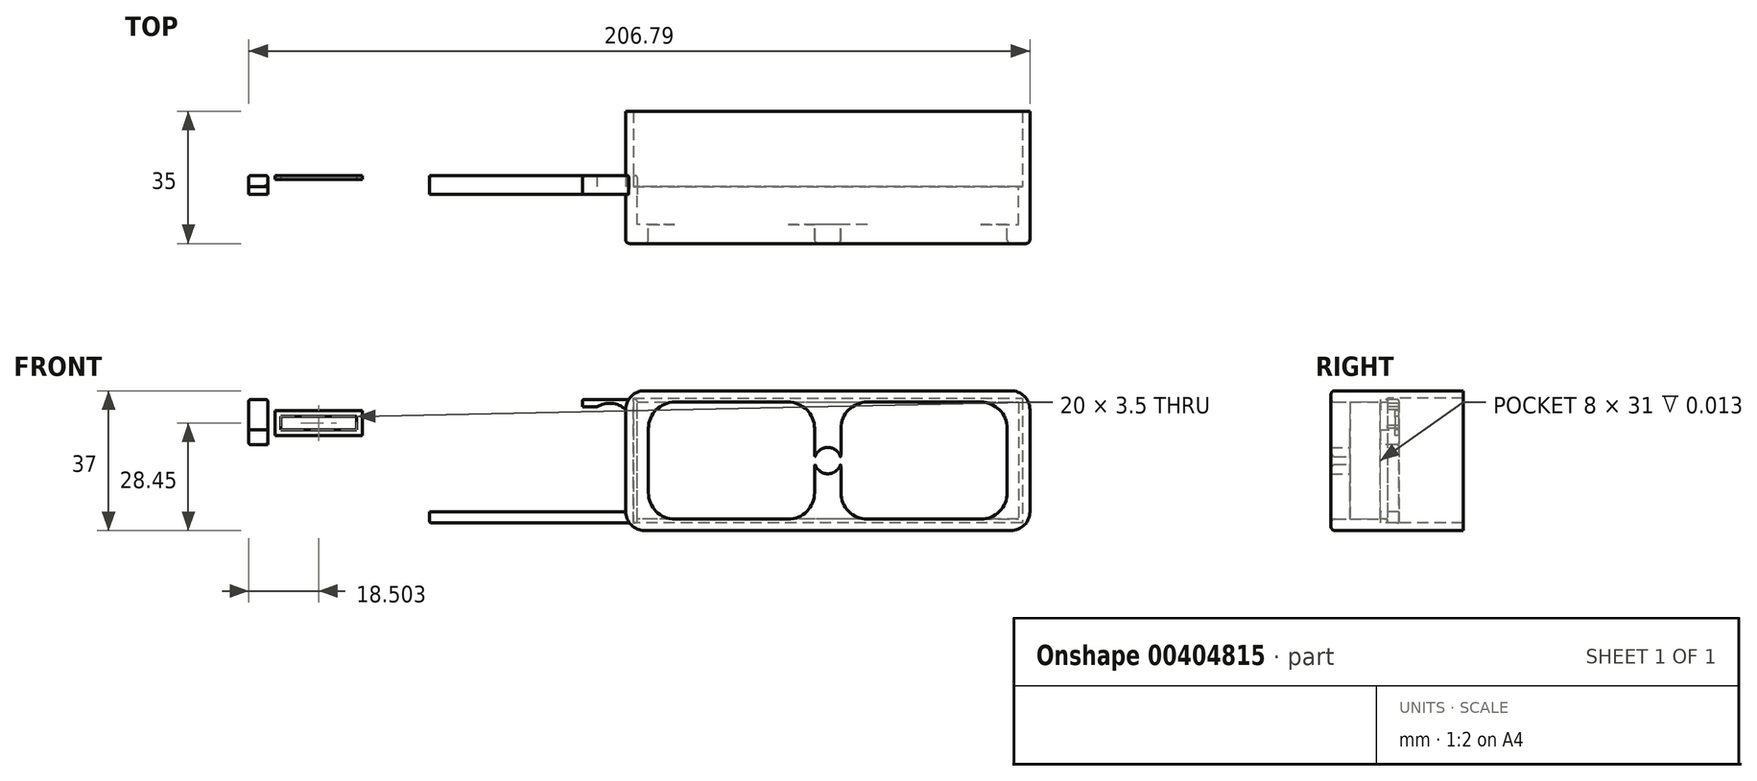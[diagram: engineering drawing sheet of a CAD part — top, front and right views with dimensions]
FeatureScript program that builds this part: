
annotation { "Feature Type Name" : "Feature", "Feature Type Description" : "" }
export const myFeature = defineFeature(function(context is Context, id is Id, definition is map)
    precondition{}
    {
        {
            var Q0;
            Q0=qCreatedBy(makeId("Front.planeOp"),FACE);
            var sketch = newSketch(context, id + "F0", { "sketchPlane" : qUnion([Q0])});
            skLineSegment(sketch, "E0", {"start": v(0, 0) * mm, "end": v(0, 33) * mm});
            skLineSegment(sketch, "E1", {"start": v(0, 33) * mm, "end": v(103, 33) * mm});
            skLineSegment(sketch, "E2", {"start": v(103, 33) * mm, "end": v(103, 0) * mm});
            skLineSegment(sketch, "E3", {"start": v(103, 0) * mm, "end": v(0, 0) * mm});
            skLineSegment(sketch, "E4.0", {"start": v(-2, -2) * mm, "end": v(-2, 35) * mm});
            skLineSegment(sketch, "E4.1", {"start": v(105, -2) * mm, "end": v(-2, -2) * mm});
            skLineSegment(sketch, "E4.2", {"start": v(105, 35) * mm, "end": v(105, -2) * mm});
            skLineSegment(sketch, "E4.3", {"start": v(-2, 35) * mm, "end": v(105, 35) * mm});
            skLineSegment(sketch, "E5", {"start": v(105, 35) * mm, "end": v(56.95, 35) * mm});
            skLineSegment(sketch, "E6", {"start": v(51.5, 33) * mm, "end": v(51.5, 20) * mm});
            skArc(sketch, "E7", {"start": v(54.85, 17.5) * mm, "mid": v(51.5, 20) * mm, "end": v(48.15, 17.5) * mm});
            skLineSegment(sketch, "E8", {"start": v(48, 17.5) * mm, "end": v(48, 25) * mm});
            skLineSegment(sketch, "E9.MirrorCS", {"start": v(55, 17.5) * mm, "end": v(55, 25) * mm});
            skLineSegment(sketch, "E10", {"start": v(48, 15.5) * mm, "end": v(48, 8) * mm});
            skLineSegment(sketch, "E11", {"start": v(55, 15.5) * mm, "end": v(55, 8) * mm});
            skLineSegment(sketch, "E12.0", {"start": v(48, 15.5) * mm, "end": v(48.15, 15.5) * mm});
            skLineSegment(sketch, "E13.0", {"start": v(48, 17.5) * mm, "end": v(48.15, 17.5) * mm});
            skArc(sketch, "E14.trimOffspring", {"start": v(48.15, 15.5) * mm, "mid": v(51.5, 13) * mm, "end": v(54.85, 15.5) * mm});
            skLineSegment(sketch, "E15.trimOffspring", {"start": v(54.85, 15.5) * mm, "end": v(55, 15.5) * mm});
            skLineSegment(sketch, "E16.trimOffspring", {"start": v(51.5, 13) * mm, "end": v(51.5, 0) * mm});
            skPoint(sketch, "E17.orphan", {"position": v(48, 16.5) * mm});
            skPoint(sketch, "E18.end.orphan", {"position": v(55, 16.5) * mm});
            skLineSegment(sketch, "E19.trimOffspring", {"start": v(54.85, 17.5) * mm, "end": v(55, 17.5) * mm});
            skLineSegment(sketch, "E20.0", {"start": v(11, 32) * mm, "end": v(41, 32) * mm});
            skLineSegment(sketch, "E20.1", {"start": v(1, 1) * mm, "end": v(1, 32) * mm});
            skLineSegment(sketch, "E20.2", {"start": v(92, 1) * mm, "end": v(62, 1) * mm});
            skLineSegment(sketch, "E20.3", {"start": v(102, 32) * mm, "end": v(102, 1) * mm});
            skLineSegment(sketch, "E21.0", {"start": v(4, 8) * mm, "end": v(4, 25) * mm});
            skLineSegment(sketch, "E22.0", {"start": v(99, 25) * mm, "end": v(99, 8) * mm});
            skArc(sketch, "E23.filletArc", {"start": v(99, 25) * mm, "mid": v(96.95, 29.95) * mm, "end": v(92, 32) * mm});
            skArc(sketch, "E24.filletArc", {"start": v(92, 1) * mm, "mid": v(96.95, 3.05) * mm, "end": v(99, 8) * mm});
            skLineSegment(sketch, "E25.trimOffspring", {"start": v(62, 32) * mm, "end": v(92, 32) * mm});
            skLineSegment(sketch, "E26.trimOffspring", {"start": v(41, 1) * mm, "end": v(11, 1) * mm});
            skArc(sketch, "E27.filletArc", {"start": v(55, 8) * mm, "mid": v(57.05, 3.05) * mm, "end": v(62, 1) * mm});
            skPoint(sketch, "E28.newPointA", {"position": v(55, 33) * mm});
            skArc(sketch, "E28.filletArc", {"start": v(62, 32) * mm, "mid": v(57.05, 29.95) * mm, "end": v(55, 25) * mm});
            skPoint(sketch, "E29.newPointA", {"position": v(48, 33) * mm});
            skArc(sketch, "E29.filletArc", {"start": v(48, 25) * mm, "mid": v(45.95, 29.95) * mm, "end": v(41, 32) * mm});
            skPoint(sketch, "E30.newPointA", {"position": v(48, 0) * mm});
            skArc(sketch, "E30.filletArc", {"start": v(41, 1) * mm, "mid": v(45.95, 3.05) * mm, "end": v(48, 8) * mm});
            skArc(sketch, "E31.filletArc", {"start": v(4, 8) * mm, "mid": v(6.05, 3.05) * mm, "end": v(11, 1) * mm});
            skArc(sketch, "E32.filletArc", {"start": v(11, 32) * mm, "mid": v(6.05, 29.95) * mm, "end": v(4, 25) * mm});
            skLineSegment(sketch, "E33", {"start": v(92, 1) * mm, "end": v(102, 1) * mm});
            skLineSegment(sketch, "E34", {"start": v(92, 32) * mm, "end": v(102, 32) * mm});
            skLineSegment(sketch, "E35", {"start": v(11, 1) * mm, "end": v(1, 1) * mm});
            skLineSegment(sketch, "E36", {"start": v(1, 32) * mm, "end": v(11, 32) * mm});
            skLineSegment(sketch, "E37", {"start": v(41, 32) * mm, "end": v(62, 32) * mm});
            skLineSegment(sketch, "E38", {"start": v(62, 1) * mm, "end": v(41, 1) * mm});
            skSolve(sketch);
        }
        {
            var Q0;
            Q0=makeQuery(id+"F0.imprint","IMPRINT",FACE,{"disambiguationData":[TD([[makeQuery(id+"F0.imprint","IMPRINT",EDGE,{"derivedFrom":sQuery(id+"F0.wireOp",EDGE,"E0")}),1.0]])]});
            extrude(context, id + "F1", {"entities" : qUnion([Q0]), "oppositeDirection" : true, "depth" : 20 * mm});
        }
        {
            var Q0;
            Q0=makeQuery(id+"F0.imprint","IMPRINT",FACE,{"disambiguationData":[TD([[makeQuery(id+"F0.imprint","IMPRINT",EDGE,{"derivedFrom":sQuery(id+"F0.wireOp",EDGE,"E0")}),1.0]])]});
            var Q1;
            Q1=makeQuery(id+"F0.imprint","IMPRINT",FACE,{"disambiguationData":[TD([[makeQuery(id+"F0.imprint","IMPRINT",EDGE,{"derivedFrom":sQuery(id+"F0.wireOp",EDGE,"E0")}),-1.0]])]});
            var Q2;
            {var subQ0=sQuery(id+"F0.wireOp",EDGE,"E13.0");Q2=makeQuery(id+"F0.imprint","IMPRINT",FACE,{"disambiguationData":[TD([[makeQuery(id+"F0.imprint","IMPRINT",EDGE,{"derivedFrom":subQ0}),1.0]])]});}
            var Q3;
            {var subQ3=sQuery(id+"F0.wireOp",EDGE,"E19.trimOffspring");Q3=makeQuery(id+"F0.imprint","IMPRINT",FACE,{"disambiguationData":[TD([[makeQuery(id+"F0.imprint","IMPRINT",EDGE,{"derivedFrom":subQ3}),1.0]])]});}
            var Q4;
            {var subQ0=sQuery(id+"F0.wireOp",EDGE,"E6");var subQ1=sQuery(id+"F0.wireOp",EDGE,"E1");var subQ2=makeQuery(id+"F0.imprint","INTERSECT",VERTEX,{"derivedFrom":[subQ1,subQ0]});Q4=makeQuery(id+"F0.imprint","IMPRINT",FACE,{"disambiguationData":[TD([[makeQuery(id+"F0.imprint","IMPRINT",EDGE,{"disambiguationData":[TD([[subQ2,1.0]])],"derivedFrom":subQ1}),-1.0]])]});}
            var Q5;
            {var subQ0=sQuery(id+"F0.wireOp",EDGE,"E6");var subQ1=sQuery(id+"F0.wireOp",EDGE,"E1");var subQ2=makeQuery(id+"F0.imprint","INTERSECT",VERTEX,{"derivedFrom":[subQ1,subQ0]});Q5=makeQuery(id+"F0.imprint","IMPRINT",FACE,{"disambiguationData":[TD([[makeQuery(id+"F0.imprint","IMPRINT",EDGE,{"disambiguationData":[TD([[subQ2,-1.0]])],"derivedFrom":subQ1}),-1.0]])]});}
            var Q6;
            {var subQ1=sQuery(id+"F0.wireOp",EDGE,"E2");Q6=makeQuery(id+"F0.imprint","IMPRINT",FACE,{"disambiguationData":[TD([[makeQuery(id+"F0.imprint","IMPRINT",EDGE,{"derivedFrom":subQ1}),-1.0]])]});}
            var Q7;
            {var subQ0=sQuery(id+"F0.wireOp",EDGE,"E11");var subQ1=sQuery(id+"F0.wireOp",EDGE,"E3");var subQ2=makeQuery(id+"F0.imprint","INTERSECT",VERTEX,{"derivedFrom":[subQ1,subQ0]});Q7=makeQuery(id+"F0.imprint","IMPRINT",FACE,{"disambiguationData":[TD([[makeQuery(id+"F0.imprint","IMPRINT",EDGE,{"disambiguationData":[TD([[subQ2,-1.0]])],"derivedFrom":subQ1}),-1.0]])]});}
            var Q8;
            {var subQ0=sQuery(id+"F0.wireOp",EDGE,"E10");var subQ1=sQuery(id+"F0.wireOp",EDGE,"E3");var subQ2=makeQuery(id+"F0.imprint","INTERSECT",VERTEX,{"derivedFrom":[subQ1,subQ0]});Q8=makeQuery(id+"F0.imprint","IMPRINT",FACE,{"disambiguationData":[TD([[makeQuery(id+"F0.imprint","IMPRINT",EDGE,{"disambiguationData":[TD([[subQ2,1.0]])],"derivedFrom":subQ1}),-1.0]])]});}
            var Q9;
            {var subQ1=sQuery(id+"F0.wireOp",EDGE,"E12.0");Q9=makeQuery(id+"F0.imprint","IMPRINT",FACE,{"disambiguationData":[TD([[makeQuery(id+"F0.imprint","IMPRINT",EDGE,{"derivedFrom":subQ1}),-1.0]])]});}
            var Q10;
            {var subQ0=sQuery(id+"F0.wireOp",EDGE,"E15.trimOffspring");Q10=makeQuery(id+"F0.imprint","IMPRINT",FACE,{"disambiguationData":[TD([[makeQuery(id+"F0.imprint","IMPRINT",EDGE,{"derivedFrom":subQ0}),-1.0]])]});}
            var Q11;
            {var subQ3=sQuery(id+"F0.wireOp",EDGE,"E9.MirrorCS");var subQ5=sQuery(id+"F0.wireOp",EDGE,"c4ed635b-4b4c-45bc-97a5-dd19808a82bc.0");var subQ6=makeQuery(id+"F0.imprint","INTERSECT",VERTEX,{"derivedFrom":[subQ5,subQ3]});Q11=makeQuery(id+"F0.imprint","IMPRINT",FACE,{"disambiguationData":[TD([[makeQuery(id+"F0.imprint","IMPRINT",EDGE,{"disambiguationData":[TD([[subQ6,-1.0]])],"derivedFrom":subQ5}),1.0]])]});}
            var Q12;
            {var subQ0=sQuery(id+"F0.wireOp",EDGE,"mgFIaH3y-DYaz-jSyi-80Px-iEue0ywse0mG");Q12=makeQuery(id+"F0.imprint","IMPRINT",FACE,{"disambiguationData":[TD([[makeQuery(id+"F0.imprint","IMPRINT",EDGE,{"derivedFrom":subQ0}),1.0]])]});}
            var Q13;
            {var subQ0=sQuery(id+"F0.wireOp",EDGE,"TVL4aVtS-kMOh-BYX0-d90f-hvQNaALXqrT4");var subQ1=sQuery(id+"F0.wireOp",EDGE,"c4ed635b-4b4c-45bc-97a5-dd19808a82bc.0");var subQ2=makeQuery(id+"F0.imprint","INTERSECT",VERTEX,{"disambiguationData":[OD(0.0)],"derivedFrom":[subQ1,subQ0]});Q13=makeQuery(id+"F0.imprint","IMPRINT",FACE,{"disambiguationData":[TD([[makeQuery(id+"F0.imprint","IMPRINT",EDGE,{"disambiguationData":[TD([[subQ2,-1.0]])],"derivedFrom":subQ1}),1.0]])]});}
            var Q14;
            {var subQ0=sQuery(id+"F0.wireOp",EDGE,"iUmxAfeH-Jdle-Fr7V-BVZL-PfV18QycgyKM");var subQ1=sQuery(id+"F0.wireOp",EDGE,"c4ed635b-4b4c-45bc-97a5-dd19808a82bc.0");var subQ2=makeQuery(id+"F0.imprint","INTERSECT",VERTEX,{"derivedFrom":[subQ1,subQ0]});Q14=makeQuery(id+"F0.imprint","IMPRINT",FACE,{"disambiguationData":[TD([[makeQuery(id+"F0.imprint","IMPRINT",EDGE,{"disambiguationData":[TD([[subQ2,-1.0]])],"derivedFrom":subQ1}),1.0]])]});}
            var Q15;
            {var subQ0=sQuery(id+"F0.wireOp",EDGE,"TVL4aVtS-kMOh-BYX0-d90f-hvQNaALXqrT4");var subQ1=sQuery(id+"F0.wireOp",EDGE,"a24374ab-3477-4681-9d0b-ab59828270b6.0");var subQ2=makeQuery(id+"F0.imprint","INTERSECT",VERTEX,{"disambiguationData":[OD(0.0)],"derivedFrom":[subQ1,subQ0]});Q15=makeQuery(id+"F0.imprint","IMPRINT",FACE,{"disambiguationData":[TD([[makeQuery(id+"F0.imprint","IMPRINT",EDGE,{"disambiguationData":[TD([[subQ2,-1.0]])],"derivedFrom":subQ1}),1.0]])]});}
            var Q16;
            {var subQ9=sQuery(id+"F0.wireOp",EDGE,"yKWUyqlz-4vPE-V50E-0xoB-uYDKYFQVyidN");Q16=makeQuery(id+"F0.imprint","IMPRINT",FACE,{"disambiguationData":[TD([[makeQuery(id+"F0.imprint","IMPRINT",EDGE,{"derivedFrom":subQ9}),1.0]])]});}
            var Q17;
            {var subQ0=sQuery(id+"F0.wireOp",EDGE,"E20.1");Q17=makeQuery(id+"F0.imprint","IMPRINT",FACE,{"disambiguationData":[TD([[makeQuery(id+"F0.imprint","IMPRINT",EDGE,{"derivedFrom":subQ0}),-1.0]])]});}
            var Q18;
            Q18=makeQuery(id+"F0.imprint","IMPRINT",FACE,{"disambiguationData":[TD([[makeQuery(id+"F0.imprint","IMPRINT",EDGE,{"derivedFrom":sQuery(id+"F0.wireOp",EDGE,"E20.3")}),-1.0]])]});
            extrude(context, id + "F2", {"entities" : qUnion([Q0, Q1, Q2, Q3, Q4, Q5, Q6, Q7, Q8, Q9, Q10, Q11, Q12, Q13, Q14, Q15, Q16, Q17, Q18]), "operationType" : NewBodyOperationType.ADD, "depth" : 15 * mm});
        }
        {
            var Q0;
            {var subQ1=sQuery(id+"F0.wireOp",EDGE,"E12.0");Q0=makeQuery(id+"F0.imprint","IMPRINT",FACE,{"disambiguationData":[TD([[makeQuery(id+"F0.imprint","IMPRINT",EDGE,{"derivedFrom":subQ1}),-1.0]])]});}
            var Q1;
            {var subQ5=sQuery(id+"F0.wireOp",EDGE,"E15.trimOffspring");Q1=makeQuery(id+"F0.imprint","IMPRINT",FACE,{"disambiguationData":[TD([[makeQuery(id+"F0.imprint","IMPRINT",EDGE,{"derivedFrom":subQ5}),-1.0]])]});}
            var Q2;
            {var subQ0=sQuery(id+"F0.wireOp",EDGE,"E19.trimOffspring");Q2=makeQuery(id+"F0.imprint","IMPRINT",FACE,{"disambiguationData":[TD([[makeQuery(id+"F0.imprint","IMPRINT",EDGE,{"derivedFrom":subQ0}),1.0]])]});}
            var Q3;
            {var subQ0=sQuery(id+"F0.wireOp",EDGE,"E13.0");Q3=makeQuery(id+"F0.imprint","IMPRINT",FACE,{"disambiguationData":[TD([[makeQuery(id+"F0.imprint","IMPRINT",EDGE,{"derivedFrom":subQ0}),1.0]])]});}
            var Q4;
            {var subQ0=sQuery(id+"F0.wireOp",EDGE,"E12.0");Q4=makeQuery(id+"F0.imprint","IMPRINT",FACE,{"disambiguationData":[TD([[makeQuery(id+"F0.imprint","IMPRINT",EDGE,{"derivedFrom":subQ0}),1.0]])]});}
            var Q5;
            Q5=makeQuery(id+"F0.imprint","IMPRINT",FACE,{"disambiguationData":[TD([[makeQuery(id+"F0.imprint","IMPRINT",EDGE,{"derivedFrom":sQuery(id+"F0.wireOp",EDGE,"E20.3")}),-1.0]])]});
            var Q6;
            Q6=makeQuery(id+"F0.imprint","IMPRINT",FACE,{"disambiguationData":[TD([[makeQuery(id+"F0.imprint","IMPRINT",EDGE,{"derivedFrom":sQuery(id+"F0.wireOp",EDGE,"E20.1")}),-1.0]])]});
            extrude(context, id + "F3", {"entities" : qUnion([Q0, Q1, Q2, Q3, Q4, Q5, Q6]), "operationType" : NewBodyOperationType.REMOVE, "depth" : 10 * mm});
        }
        {
            var Q0;
            Q0=makeQuery(id+"F2.opExtrude","SWEPT_EDGE",EDGE,{"disambiguationData":[OSD([sQuery(id+"F0.wireOp",EDGE,"E20.0"),sQuery(id+"F0.wireOp",EDGE,"E20.1")])]});
            var Q1;
            Q1=makeQuery(id+"F2.opExtrude","SWEPT_EDGE",EDGE,{"disambiguationData":[OSD([sQuery(id+"F0.wireOp",EDGE,"E8"),sQuery(id+"F0.wireOp",EDGE,"E20.0")])]});
            var Q2;
            Q2=makeQuery(id+"F2.opExtrude","SWEPT_EDGE",EDGE,{"disambiguationData":[OSD([sQuery(id+"F0.wireOp",EDGE,"E11"),sQuery(id+"F0.wireOp",EDGE,"E20.2")])]});
            var Q3;
            Q3=makeQuery(id+"F2.opExtrude","SWEPT_EDGE",EDGE,{"disambiguationData":[OSD([sQuery(id+"F0.wireOp",EDGE,"E20.1"),sQuery(id+"F0.wireOp",EDGE,"E20.2")])]});
            var Q4;
            Q4=makeQuery(id+"F2.opExtrude","SWEPT_EDGE",EDGE,{"disambiguationData":[OSD([sQuery(id+"F0.wireOp",EDGE,"E10"),sQuery(id+"F0.wireOp",EDGE,"E20.2")])]});
            var Q5;
            Q5=makeQuery(id+"F2.opExtrude","SWEPT_EDGE",EDGE,{"disambiguationData":[OSD([sQuery(id+"F0.wireOp",EDGE,"E20.2"),sQuery(id+"F0.wireOp",EDGE,"E20.3")])]});
            var Q6;
            Q6=makeQuery(id+"F2.opExtrude","SWEPT_EDGE",EDGE,{"disambiguationData":[OSD([sQuery(id+"F0.wireOp",EDGE,"E20.0"),sQuery(id+"F0.wireOp",EDGE,"E20.3")])]});
            var Q7;
            {var subQ0=sQuery(id+"F0.wireOp",EDGE,"E4.2");var subQ1=sQuery(id+"F0.wireOp",EDGE,"E4.1");Q7=makeQuery(id+"F2.boolean.opBoolean","MERGE",EDGE,{"derivedFrom":[makeQuery(id+"F1.opExtrude","SWEPT_EDGE",EDGE,{"disambiguationData":[OSD([subQ1,subQ0])]}),makeQuery(id+"F2.opExtrude","SWEPT_EDGE",EDGE,{"disambiguationData":[OSD([subQ1,subQ0])]})]});}
            var Q8;
            {var subQ0=sQuery(id+"F0.wireOp",EDGE,"E5");var subQ1=sQuery(id+"F0.wireOp",EDGE,"E4.2");Q8=makeQuery(id+"F2.boolean.opBoolean","MERGE",EDGE,{"derivedFrom":[makeQuery(id+"F1.opExtrude","SWEPT_EDGE",EDGE,{"disambiguationData":[OSD([subQ1,subQ0])]}),makeQuery(id+"F2.opExtrude","SWEPT_EDGE",EDGE,{"disambiguationData":[OSD([subQ1,subQ0])]})]});}
            var Q9;
            {var subQ0=sQuery(id+"F0.wireOp",EDGE,"E4.3");var subQ1=sQuery(id+"F0.wireOp",EDGE,"E4.0");Q9=makeQuery(id+"F2.boolean.opBoolean","MERGE",EDGE,{"derivedFrom":[makeQuery(id+"F1.opExtrude","SWEPT_EDGE",EDGE,{"disambiguationData":[OSD([subQ1,subQ0])]}),makeQuery(id+"F2.opExtrude","SWEPT_EDGE",EDGE,{"disambiguationData":[OSD([subQ1,subQ0])]})]});}
            var Q10;
            {var subQ0=sQuery(id+"F0.wireOp",EDGE,"E4.1");var subQ1=sQuery(id+"F0.wireOp",EDGE,"E4.0");Q10=makeQuery(id+"F2.boolean.opBoolean","MERGE",EDGE,{"derivedFrom":[makeQuery(id+"F1.opExtrude","SWEPT_EDGE",EDGE,{"disambiguationData":[OSD([subQ1,subQ0])]}),makeQuery(id+"F2.opExtrude","SWEPT_EDGE",EDGE,{"disambiguationData":[OSD([subQ1,subQ0])]})]});}
            var Q11;
            Q11=makeQuery(id+"F2.opExtrude","SWEPT_EDGE",EDGE,{"disambiguationData":[OSD([sQuery(id+"F0.wireOp",EDGE,"E9.MirrorCS"),sQuery(id+"F0.wireOp",EDGE,"E20.0")])]});
            fillet(context, id + "F4", {"entities" : qUnion([Q0, Q1, Q2, Q3, Q4, Q5, Q6, Q7, Q8, Q9, Q10, Q11]), "radius" : 5 * mm, "tangentPropagation" : true, "allowEdgeOverflow" : false});
        }
        {
            var Q0;
            Q0=makeQuery(id+"F2.opExtrude","CAP_EDGE",EDGE,{"disambiguationData":[OSD([sQuery(id+"F0.wireOp",EDGE,"E32.filletArc")])],"isStart":false});
            var Q1;
            Q1=makeQuery(id+"F2.opExtrude","CAP_EDGE",EDGE,{"disambiguationData":[OSD([sQuery(id+"F0.wireOp",EDGE,"E28.filletArc")])],"isStart":false});
            var Q2;
            Q2=makeQuery(id+"F2.opExtrude","CAP_EDGE",EDGE,{"disambiguationData":[OSD([sQuery(id+"F0.wireOp",EDGE,"E4.3"),sQuery(id+"F0.wireOp",EDGE,"E5")])],"isStart":false});
            var Q3;
            Q3=makeQuery(id+"F1ZY5U0QfWKgnaE_2.boolean.opBoolean","COPY",EDGE,{"derivedFrom":makeQuery(id+"F1ZY5U0QfWKgnaE_2.opExtrude","CAP_EDGE",EDGE,{"disambiguationData":[OSD([sQuery(id+"FzWsDeid9OxCe4s_2.wireOp",EDGE,"ddf2c67c-9696-4573-b7c7-edc6250c991e.0")])],"isStart":true})});
            var Q4;
            {var subQ0=sQuery(id+"FzWsDeid9OxCe4s_2.wireOp",EDGE,"DHWVtWLh-aHPT-YNDw-NuMh-FcVQlgM1t4xD");Q4=makeQuery(id+"F1ZY5U0QfWKgnaE_2.boolean.opBoolean","COPY",EDGE,{"derivedFrom":makeQuery(id+"F1ZY5U0QfWKgnaE_2.opExtrude","CAP_EDGE",EDGE,{"disambiguationData":[OSD([subQ0]),TDD([makeQuery(id+"FzWsDeid9OxCe4s_2.imprint","IMPRINT",EDGE,{"disambiguationData":[TD([[makeQuery(id+"FzWsDeid9OxCe4s_2.imprint","INTERSECT",VERTEX,{"derivedFrom":[subQ0,sQuery(id+"FzWsDeid9OxCe4s_2.wireOp",EDGE,"ddf2c67c-9696-4573-b7c7-edc6250c991e.0")]}),-1.0]])],"derivedFrom":subQ0})])],"isStart":true})});}
            var Q5;
            {var subQ0=sQuery(id+"FzWsDeid9OxCe4s_2.wireOp",EDGE,"uo2K4ESE-ioYr-gu5B-DHa5-rfcAboMNfEFw");Q5=makeQuery(id+"F1ZY5U0QfWKgnaE_2.boolean.opBoolean","COPY",EDGE,{"derivedFrom":makeQuery(id+"F1ZY5U0QfWKgnaE_2.opExtrude","CAP_EDGE",EDGE,{"disambiguationData":[OSD([subQ0]),TDD([makeQuery(id+"FzWsDeid9OxCe4s_2.imprint","IMPRINT",EDGE,{"disambiguationData":[TD([[makeQuery(id+"FzWsDeid9OxCe4s_2.imprint","INTERSECT",VERTEX,{"derivedFrom":[subQ0,sQuery(id+"FzWsDeid9OxCe4s_2.wireOp",EDGE,"ddf2c67c-9696-4573-b7c7-edc6250c991e.0")]}),1.0]])],"derivedFrom":subQ0})])],"isStart":true})});}
            var Q6;
            Q6=makeQuery(id+"F1ZY5U0QfWKgnaE_2.boolean.opBoolean","COPY",EDGE,{"derivedFrom":makeQuery(id+"F1ZY5U0QfWKgnaE_2.opExtrude","CAP_EDGE",EDGE,{"disambiguationData":[OSD([sQuery(id+"FzWsDeid9OxCe4s_2.wireOp",EDGE,"6cb0e26c-a951-431f-a703-2220c8751553.0")])],"isStart":true})});
            var Q7;
            Q7=makeQuery(id+"F1ZY5U0QfWKgnaE_2.boolean.opBoolean","COPY",EDGE,{"derivedFrom":makeQuery(id+"F1ZY5U0QfWKgnaE_2.opExtrude","CAP_EDGE",EDGE,{"disambiguationData":[OSD([sQuery(id+"FzWsDeid9OxCe4s_2.wireOp",EDGE,"f3bd379a-a156-41d0-9f10-f2bbd5b9d83f.0")])],"isStart":true})});
            var Q8;
            {var subQ0=sQuery(id+"FzWsDeid9OxCe4s_2.wireOp",EDGE,"uo2K4ESE-ioYr-gu5B-DHa5-rfcAboMNfEFw");Q8=makeQuery(id+"F1ZY5U0QfWKgnaE_2.boolean.opBoolean","COPY",EDGE,{"derivedFrom":makeQuery(id+"F1ZY5U0QfWKgnaE_2.opExtrude","CAP_EDGE",EDGE,{"disambiguationData":[OSD([subQ0]),TDD([makeQuery(id+"FzWsDeid9OxCe4s_2.imprint","IMPRINT",EDGE,{"disambiguationData":[TD([[makeQuery(id+"FzWsDeid9OxCe4s_2.imprint","INTERSECT",VERTEX,{"derivedFrom":[subQ0,sQuery(id+"FzWsDeid9OxCe4s_2.wireOp",EDGE,"f3bd379a-a156-41d0-9f10-f2bbd5b9d83f.0")]}),-1.0]])],"derivedFrom":subQ0})])],"isStart":true})});}
            var Q9;
            {var subQ0=sQuery(id+"FzWsDeid9OxCe4s_2.wireOp",EDGE,"DHWVtWLh-aHPT-YNDw-NuMh-FcVQlgM1t4xD");Q9=makeQuery(id+"F1ZY5U0QfWKgnaE_2.boolean.opBoolean","COPY",EDGE,{"derivedFrom":makeQuery(id+"F1ZY5U0QfWKgnaE_2.opExtrude","CAP_EDGE",EDGE,{"disambiguationData":[OSD([subQ0]),TDD([makeQuery(id+"FzWsDeid9OxCe4s_2.imprint","IMPRINT",EDGE,{"disambiguationData":[TD([[makeQuery(id+"FzWsDeid9OxCe4s_2.imprint","INTERSECT",VERTEX,{"derivedFrom":[subQ0,sQuery(id+"FzWsDeid9OxCe4s_2.wireOp",EDGE,"f3bd379a-a156-41d0-9f10-f2bbd5b9d83f.0")]}),1.0]])],"derivedFrom":subQ0})])],"isStart":true})});}
            var Q10;
            Q10=makeQuery(id+"F1ZY5U0QfWKgnaE_2.boolean.opBoolean","COPY",EDGE,{"derivedFrom":makeQuery(id+"F1ZY5U0QfWKgnaE_2.opExtrude","CAP_EDGE",EDGE,{"disambiguationData":[OSD([sQuery(id+"FzWsDeid9OxCe4s_2.wireOp",EDGE,"52b8b0e7-0203-483f-8d4f-d96776e66651.0")])],"isStart":true})});
            var Q11;
            {var subQ0=sQuery(id+"FzWsDeid9OxCe4s_2.wireOp",EDGE,"DHWVtWLh-aHPT-YNDw-NuMh-FcVQlgM1t4xD");var subQ1=sQuery(id+"F0.wireOp",EDGE,"E4.1");Q11=makeQuery(id+"F1ZY5U0QfWKgnaE_2.boolean.opBoolean","INTERSECT",EDGE,{"derivedFrom":[makeQuery(id+"F2.boolean.opBoolean","MERGE",FACE,{"derivedFrom":[makeQuery(id+"F1.opExtrude","SWEPT_FACE",FACE,{"disambiguationData":[OSD([subQ1])]}),makeQuery(id+"F2.opExtrude","SWEPT_FACE",FACE,{"disambiguationData":[OSD([subQ1])]})]}),makeQuery(id+"F1ZY5U0QfWKgnaE_2.opExtrude","SWEPT_FACE",FACE,{"disambiguationData":[OSD([subQ0]),TDD([makeQuery(id+"FzWsDeid9OxCe4s_2.imprint","IMPRINT",EDGE,{"disambiguationData":[TD([[makeQuery(id+"FzWsDeid9OxCe4s_2.imprint","INTERSECT",VERTEX,{"derivedFrom":[subQ0,sQuery(id+"FzWsDeid9OxCe4s_2.wireOp",EDGE,"f3bd379a-a156-41d0-9f10-f2bbd5b9d83f.0")]}),1.0]])],"derivedFrom":subQ0})])]})]});}
            var Q12;
            {var subQ0=sQuery(id+"FzWsDeid9OxCe4s_2.wireOp",EDGE,"DHWVtWLh-aHPT-YNDw-NuMh-FcVQlgM1t4xD");var subQ1=sQuery(id+"F0.wireOp",EDGE,"E4.1");Q12=makeQuery(id+"F1ZY5U0QfWKgnaE_2.boolean.opBoolean","INTERSECT",EDGE,{"derivedFrom":[makeQuery(id+"F2.boolean.opBoolean","MERGE",FACE,{"derivedFrom":[makeQuery(id+"F1.opExtrude","SWEPT_FACE",FACE,{"disambiguationData":[OSD([subQ1])]}),makeQuery(id+"F2.opExtrude","SWEPT_FACE",FACE,{"disambiguationData":[OSD([subQ1])]})]}),makeQuery(id+"F1ZY5U0QfWKgnaE_2.opExtrude","SWEPT_FACE",FACE,{"disambiguationData":[OSD([subQ0]),TDD([makeQuery(id+"FzWsDeid9OxCe4s_2.imprint","IMPRINT",EDGE,{"disambiguationData":[TD([[makeQuery(id+"FzWsDeid9OxCe4s_2.imprint","INTERSECT",VERTEX,{"derivedFrom":[subQ0,sQuery(id+"FzWsDeid9OxCe4s_2.wireOp",EDGE,"f3bd379a-a156-41d0-9f10-f2bbd5b9d83f.0")]}),1.0]])],"derivedFrom":subQ0})])]})]});}
            var Q13;
            {var subQ0=sQuery(id+"F0.wireOp",EDGE,"E4.1");Q13=makeQuery(id+"F1ZY5U0QfWKgnaE_2.boolean.opBoolean","INTERSECT",EDGE,{"derivedFrom":[makeQuery(id+"F2.boolean.opBoolean","MERGE",FACE,{"derivedFrom":[makeQuery(id+"F1.opExtrude","SWEPT_FACE",FACE,{"disambiguationData":[OSD([subQ0])]}),makeQuery(id+"F2.opExtrude","SWEPT_FACE",FACE,{"disambiguationData":[OSD([subQ0])]})]}),makeQuery(id+"F1ZY5U0QfWKgnaE_2.opExtrude","SWEPT_FACE",FACE,{"disambiguationData":[OSD([sQuery(id+"FzWsDeid9OxCe4s_2.wireOp",EDGE,"f3bd379a-a156-41d0-9f10-f2bbd5b9d83f.0")])]})]});}
            var Q14;
            {var subQ0=sQuery(id+"FzWsDeid9OxCe4s_2.wireOp",EDGE,"uo2K4ESE-ioYr-gu5B-DHa5-rfcAboMNfEFw");var subQ1=sQuery(id+"F0.wireOp",EDGE,"E4.1");Q14=makeQuery(id+"F1ZY5U0QfWKgnaE_2.boolean.opBoolean","INTERSECT",EDGE,{"derivedFrom":[makeQuery(id+"F2.boolean.opBoolean","MERGE",FACE,{"derivedFrom":[makeQuery(id+"F1.opExtrude","SWEPT_FACE",FACE,{"disambiguationData":[OSD([subQ1])]}),makeQuery(id+"F2.opExtrude","SWEPT_FACE",FACE,{"disambiguationData":[OSD([subQ1])]})]}),makeQuery(id+"F1ZY5U0QfWKgnaE_2.opExtrude","SWEPT_FACE",FACE,{"disambiguationData":[OSD([subQ0]),TDD([makeQuery(id+"FzWsDeid9OxCe4s_2.imprint","IMPRINT",EDGE,{"disambiguationData":[TD([[makeQuery(id+"FzWsDeid9OxCe4s_2.imprint","INTERSECT",VERTEX,{"derivedFrom":[subQ0,sQuery(id+"FzWsDeid9OxCe4s_2.wireOp",EDGE,"f3bd379a-a156-41d0-9f10-f2bbd5b9d83f.0")]}),-1.0]])],"derivedFrom":subQ0})])]})]});}
            var Q15;
            {var subQ0=sQuery(id+"F0.wireOp",EDGE,"E4.1");Q15=makeQuery(id+"F1ZY5U0QfWKgnaE_2.boolean.opBoolean","INTERSECT",EDGE,{"derivedFrom":[makeQuery(id+"F2.boolean.opBoolean","MERGE",FACE,{"derivedFrom":[makeQuery(id+"F1.opExtrude","SWEPT_FACE",FACE,{"disambiguationData":[OSD([subQ0])]}),makeQuery(id+"F2.opExtrude","SWEPT_FACE",FACE,{"disambiguationData":[OSD([subQ0])]})]}),makeQuery(id+"F1ZY5U0QfWKgnaE_2.opExtrude","SWEPT_FACE",FACE,{"disambiguationData":[OSD([sQuery(id+"FzWsDeid9OxCe4s_2.wireOp",EDGE,"52b8b0e7-0203-483f-8d4f-d96776e66651.0")])]})]});}
            var Q16;
            {var subQ0=sQuery(id+"F0.wireOp",EDGE,"E4.1");Q16=makeQuery(id+"F1ZY5U0QfWKgnaE_2.boolean.opBoolean","INTERSECT",EDGE,{"derivedFrom":[makeQuery(id+"F2.boolean.opBoolean","MERGE",FACE,{"derivedFrom":[makeQuery(id+"F1.opExtrude","SWEPT_FACE",FACE,{"disambiguationData":[OSD([subQ0])]}),makeQuery(id+"F2.opExtrude","SWEPT_FACE",FACE,{"disambiguationData":[OSD([subQ0])]})]}),makeQuery(id+"F1ZY5U0QfWKgnaE_2.opExtrude","SWEPT_FACE",FACE,{"disambiguationData":[OSD([sQuery(id+"FzWsDeid9OxCe4s_2.wireOp",EDGE,"ddf2c67c-9696-4573-b7c7-edc6250c991e.0")])]})]});}
            var Q17;
            {var subQ0=sQuery(id+"FzWsDeid9OxCe4s_2.wireOp",EDGE,"uo2K4ESE-ioYr-gu5B-DHa5-rfcAboMNfEFw");var subQ1=sQuery(id+"F0.wireOp",EDGE,"E4.1");Q17=makeQuery(id+"F1ZY5U0QfWKgnaE_2.boolean.opBoolean","INTERSECT",EDGE,{"derivedFrom":[makeQuery(id+"F2.boolean.opBoolean","MERGE",FACE,{"derivedFrom":[makeQuery(id+"F1.opExtrude","SWEPT_FACE",FACE,{"disambiguationData":[OSD([subQ1])]}),makeQuery(id+"F2.opExtrude","SWEPT_FACE",FACE,{"disambiguationData":[OSD([subQ1])]})]}),makeQuery(id+"F1ZY5U0QfWKgnaE_2.opExtrude","SWEPT_FACE",FACE,{"disambiguationData":[OSD([subQ0]),TDD([makeQuery(id+"FzWsDeid9OxCe4s_2.imprint","IMPRINT",EDGE,{"disambiguationData":[TD([[makeQuery(id+"FzWsDeid9OxCe4s_2.imprint","INTERSECT",VERTEX,{"derivedFrom":[subQ0,sQuery(id+"FzWsDeid9OxCe4s_2.wireOp",EDGE,"ddf2c67c-9696-4573-b7c7-edc6250c991e.0")]}),1.0]])],"derivedFrom":subQ0})])]})]});}
            var Q18;
            {var subQ0=sQuery(id+"F0.wireOp",EDGE,"E4.1");Q18=makeQuery(id+"F1ZY5U0QfWKgnaE_2.boolean.opBoolean","INTERSECT",EDGE,{"derivedFrom":[makeQuery(id+"F2.boolean.opBoolean","MERGE",FACE,{"derivedFrom":[makeQuery(id+"F1.opExtrude","SWEPT_FACE",FACE,{"disambiguationData":[OSD([subQ0])]}),makeQuery(id+"F2.opExtrude","SWEPT_FACE",FACE,{"disambiguationData":[OSD([subQ0])]})]}),makeQuery(id+"F1ZY5U0QfWKgnaE_2.opExtrude","SWEPT_FACE",FACE,{"disambiguationData":[OSD([sQuery(id+"FzWsDeid9OxCe4s_2.wireOp",EDGE,"6cb0e26c-a951-431f-a703-2220c8751553.0")])]})]});}
            var Q19;
            {var subQ0=sQuery(id+"FzWsDeid9OxCe4s_2.wireOp",EDGE,"DHWVtWLh-aHPT-YNDw-NuMh-FcVQlgM1t4xD");var subQ1=sQuery(id+"F0.wireOp",EDGE,"E4.1");Q19=makeQuery(id+"F1ZY5U0QfWKgnaE_2.boolean.opBoolean","INTERSECT",EDGE,{"derivedFrom":[makeQuery(id+"F2.boolean.opBoolean","MERGE",FACE,{"derivedFrom":[makeQuery(id+"F1.opExtrude","SWEPT_FACE",FACE,{"disambiguationData":[OSD([subQ1])]}),makeQuery(id+"F2.opExtrude","SWEPT_FACE",FACE,{"disambiguationData":[OSD([subQ1])]})]}),makeQuery(id+"F1ZY5U0QfWKgnaE_2.opExtrude","SWEPT_FACE",FACE,{"disambiguationData":[OSD([subQ0]),TDD([makeQuery(id+"FzWsDeid9OxCe4s_2.imprint","IMPRINT",EDGE,{"disambiguationData":[TD([[makeQuery(id+"FzWsDeid9OxCe4s_2.imprint","INTERSECT",VERTEX,{"derivedFrom":[subQ0,sQuery(id+"FzWsDeid9OxCe4s_2.wireOp",EDGE,"ddf2c67c-9696-4573-b7c7-edc6250c991e.0")]}),-1.0]])],"derivedFrom":subQ0})])]})]});}
            var Q20;
            {var subQ0=sQuery(id+"F0.wireOp",EDGE,"E1");Q20=makeQuery(id+"F1ZY5U0QfWKgnaE_2.boolean.opBoolean","INTERSECT",EDGE,{"derivedFrom":[makeQuery(id+"F3.boolean.opBoolean","MERGE",FACE,{"derivedFrom":[makeQuery(id+"F1.opExtrude","SWEPT_FACE",FACE,{"disambiguationData":[OSD([subQ0])]}),makeQuery(id+"F3.opExtrude","SWEPT_FACE",FACE,{"disambiguationData":[OSD([subQ0])]})]}),makeQuery(id+"F1ZY5U0QfWKgnaE_2.opExtrude","SWEPT_FACE",FACE,{"disambiguationData":[OSD([sQuery(id+"FzWsDeid9OxCe4s_2.wireOp",EDGE,"52b8b0e7-0203-483f-8d4f-d96776e66651.0")])]})]});}
            var Q21;
            {var subQ0=sQuery(id+"FzWsDeid9OxCe4s_2.wireOp",EDGE,"DHWVtWLh-aHPT-YNDw-NuMh-FcVQlgM1t4xD");var subQ1=sQuery(id+"F0.wireOp",EDGE,"E1");Q21=makeQuery(id+"F1ZY5U0QfWKgnaE_2.boolean.opBoolean","INTERSECT",EDGE,{"derivedFrom":[makeQuery(id+"F3.boolean.opBoolean","MERGE",FACE,{"derivedFrom":[makeQuery(id+"F1.opExtrude","SWEPT_FACE",FACE,{"disambiguationData":[OSD([subQ1])]}),makeQuery(id+"F3.opExtrude","SWEPT_FACE",FACE,{"disambiguationData":[OSD([subQ1])]})]}),makeQuery(id+"F1ZY5U0QfWKgnaE_2.opExtrude","SWEPT_FACE",FACE,{"disambiguationData":[OSD([subQ0]),TDD([makeQuery(id+"FzWsDeid9OxCe4s_2.imprint","IMPRINT",EDGE,{"disambiguationData":[TD([[makeQuery(id+"FzWsDeid9OxCe4s_2.imprint","INTERSECT",VERTEX,{"derivedFrom":[subQ0,sQuery(id+"FzWsDeid9OxCe4s_2.wireOp",EDGE,"f3bd379a-a156-41d0-9f10-f2bbd5b9d83f.0")]}),1.0]])],"derivedFrom":subQ0})])]})]});}
            var Q22;
            {var subQ0=sQuery(id+"F0.wireOp",EDGE,"E1");Q22=makeQuery(id+"F1ZY5U0QfWKgnaE_2.boolean.opBoolean","INTERSECT",EDGE,{"derivedFrom":[makeQuery(id+"F3.boolean.opBoolean","MERGE",FACE,{"derivedFrom":[makeQuery(id+"F1.opExtrude","SWEPT_FACE",FACE,{"disambiguationData":[OSD([subQ0])]}),makeQuery(id+"F3.opExtrude","SWEPT_FACE",FACE,{"disambiguationData":[OSD([subQ0])]})]}),makeQuery(id+"F1ZY5U0QfWKgnaE_2.opExtrude","SWEPT_FACE",FACE,{"disambiguationData":[OSD([sQuery(id+"FzWsDeid9OxCe4s_2.wireOp",EDGE,"f3bd379a-a156-41d0-9f10-f2bbd5b9d83f.0")])]})]});}
            var Q23;
            {var subQ0=sQuery(id+"F0.wireOp",EDGE,"E1");Q23=makeQuery(id+"F1ZY5U0QfWKgnaE_2.boolean.opBoolean","INTERSECT",EDGE,{"derivedFrom":[makeQuery(id+"F3.boolean.opBoolean","MERGE",FACE,{"derivedFrom":[makeQuery(id+"F1.opExtrude","SWEPT_FACE",FACE,{"disambiguationData":[OSD([subQ0])]}),makeQuery(id+"F3.opExtrude","SWEPT_FACE",FACE,{"disambiguationData":[OSD([subQ0])]})]}),makeQuery(id+"F1ZY5U0QfWKgnaE_2.opExtrude","SWEPT_FACE",FACE,{"disambiguationData":[OSD([sQuery(id+"FzWsDeid9OxCe4s_2.wireOp",EDGE,"ddf2c67c-9696-4573-b7c7-edc6250c991e.0")])]})]});}
            var Q24;
            {var subQ0=sQuery(id+"FzWsDeid9OxCe4s_2.wireOp",EDGE,"uo2K4ESE-ioYr-gu5B-DHa5-rfcAboMNfEFw");var subQ1=sQuery(id+"F0.wireOp",EDGE,"E1");Q24=makeQuery(id+"F1ZY5U0QfWKgnaE_2.boolean.opBoolean","INTERSECT",EDGE,{"derivedFrom":[makeQuery(id+"F3.boolean.opBoolean","MERGE",FACE,{"derivedFrom":[makeQuery(id+"F1.opExtrude","SWEPT_FACE",FACE,{"disambiguationData":[OSD([subQ1])]}),makeQuery(id+"F3.opExtrude","SWEPT_FACE",FACE,{"disambiguationData":[OSD([subQ1])]})]}),makeQuery(id+"F1ZY5U0QfWKgnaE_2.opExtrude","SWEPT_FACE",FACE,{"disambiguationData":[OSD([subQ0]),TDD([makeQuery(id+"FzWsDeid9OxCe4s_2.imprint","IMPRINT",EDGE,{"disambiguationData":[TD([[makeQuery(id+"FzWsDeid9OxCe4s_2.imprint","INTERSECT",VERTEX,{"derivedFrom":[subQ0,sQuery(id+"FzWsDeid9OxCe4s_2.wireOp",EDGE,"ddf2c67c-9696-4573-b7c7-edc6250c991e.0")]}),1.0]])],"derivedFrom":subQ0})])]})]});}
            var Q25;
            {var subQ0=sQuery(id+"FzWsDeid9OxCe4s_2.wireOp",EDGE,"DHWVtWLh-aHPT-YNDw-NuMh-FcVQlgM1t4xD");var subQ1=sQuery(id+"F0.wireOp",EDGE,"E1");Q25=makeQuery(id+"F1ZY5U0QfWKgnaE_2.boolean.opBoolean","INTERSECT",EDGE,{"derivedFrom":[makeQuery(id+"F3.boolean.opBoolean","MERGE",FACE,{"derivedFrom":[makeQuery(id+"F1.opExtrude","SWEPT_FACE",FACE,{"disambiguationData":[OSD([subQ1])]}),makeQuery(id+"F3.opExtrude","SWEPT_FACE",FACE,{"disambiguationData":[OSD([subQ1])]})]}),makeQuery(id+"F1ZY5U0QfWKgnaE_2.opExtrude","SWEPT_FACE",FACE,{"disambiguationData":[OSD([subQ0]),TDD([makeQuery(id+"FzWsDeid9OxCe4s_2.imprint","IMPRINT",EDGE,{"disambiguationData":[TD([[makeQuery(id+"FzWsDeid9OxCe4s_2.imprint","INTERSECT",VERTEX,{"derivedFrom":[subQ0,sQuery(id+"FzWsDeid9OxCe4s_2.wireOp",EDGE,"ddf2c67c-9696-4573-b7c7-edc6250c991e.0")]}),-1.0]])],"derivedFrom":subQ0})])]})]});}
            var Q26;
            {var subQ0=sQuery(id+"F0.wireOp",EDGE,"E1");Q26=makeQuery(id+"F1ZY5U0QfWKgnaE_2.boolean.opBoolean","INTERSECT",EDGE,{"derivedFrom":[makeQuery(id+"F3.boolean.opBoolean","MERGE",FACE,{"derivedFrom":[makeQuery(id+"F1.opExtrude","SWEPT_FACE",FACE,{"disambiguationData":[OSD([subQ0])]}),makeQuery(id+"F3.opExtrude","SWEPT_FACE",FACE,{"disambiguationData":[OSD([subQ0])]})]}),makeQuery(id+"F1ZY5U0QfWKgnaE_2.opExtrude","SWEPT_FACE",FACE,{"disambiguationData":[OSD([sQuery(id+"FzWsDeid9OxCe4s_2.wireOp",EDGE,"6cb0e26c-a951-431f-a703-2220c8751553.0")])]})]});}
            var Q27;
            {var subQ0=sQuery(id+"F0.wireOp",EDGE,"E3");Q27=makeQuery(id+"F1ZY5U0QfWKgnaE_2.boolean.opBoolean","INTERSECT",EDGE,{"derivedFrom":[makeQuery(id+"F3.boolean.opBoolean","MERGE",FACE,{"derivedFrom":[makeQuery(id+"F1.opExtrude","SWEPT_FACE",FACE,{"disambiguationData":[OSD([subQ0])]}),makeQuery(id+"F3.opExtrude","SWEPT_FACE",FACE,{"disambiguationData":[OSD([subQ0])]})]}),makeQuery(id+"F1ZY5U0QfWKgnaE_2.opExtrude","SWEPT_FACE",FACE,{"disambiguationData":[OSD([sQuery(id+"FzWsDeid9OxCe4s_2.wireOp",EDGE,"ddf2c67c-9696-4573-b7c7-edc6250c991e.0")])]})]});}
            var Q28;
            {var subQ0=sQuery(id+"FzWsDeid9OxCe4s_2.wireOp",EDGE,"uo2K4ESE-ioYr-gu5B-DHa5-rfcAboMNfEFw");var subQ1=sQuery(id+"F0.wireOp",EDGE,"E3");Q28=makeQuery(id+"F1ZY5U0QfWKgnaE_2.boolean.opBoolean","INTERSECT",EDGE,{"derivedFrom":[makeQuery(id+"F3.boolean.opBoolean","MERGE",FACE,{"derivedFrom":[makeQuery(id+"F1.opExtrude","SWEPT_FACE",FACE,{"disambiguationData":[OSD([subQ1])]}),makeQuery(id+"F3.opExtrude","SWEPT_FACE",FACE,{"disambiguationData":[OSD([subQ1])]})]}),makeQuery(id+"F1ZY5U0QfWKgnaE_2.opExtrude","SWEPT_FACE",FACE,{"disambiguationData":[OSD([subQ0]),TDD([makeQuery(id+"FzWsDeid9OxCe4s_2.imprint","IMPRINT",EDGE,{"disambiguationData":[TD([[makeQuery(id+"FzWsDeid9OxCe4s_2.imprint","INTERSECT",VERTEX,{"derivedFrom":[subQ0,sQuery(id+"FzWsDeid9OxCe4s_2.wireOp",EDGE,"ddf2c67c-9696-4573-b7c7-edc6250c991e.0")]}),1.0]])],"derivedFrom":subQ0})])]})]});}
            var Q29;
            {var subQ0=sQuery(id+"F0.wireOp",EDGE,"E3");Q29=makeQuery(id+"F1ZY5U0QfWKgnaE_2.boolean.opBoolean","INTERSECT",EDGE,{"derivedFrom":[makeQuery(id+"F3.boolean.opBoolean","MERGE",FACE,{"derivedFrom":[makeQuery(id+"F1.opExtrude","SWEPT_FACE",FACE,{"disambiguationData":[OSD([subQ0])]}),makeQuery(id+"F3.opExtrude","SWEPT_FACE",FACE,{"disambiguationData":[OSD([subQ0])]})]}),makeQuery(id+"F1ZY5U0QfWKgnaE_2.opExtrude","SWEPT_FACE",FACE,{"disambiguationData":[OSD([sQuery(id+"FzWsDeid9OxCe4s_2.wireOp",EDGE,"6cb0e26c-a951-431f-a703-2220c8751553.0")])]})]});}
            var Q30;
            {var subQ0=sQuery(id+"FzWsDeid9OxCe4s_2.wireOp",EDGE,"uo2K4ESE-ioYr-gu5B-DHa5-rfcAboMNfEFw");var subQ1=sQuery(id+"F0.wireOp",EDGE,"E3");Q30=makeQuery(id+"F1ZY5U0QfWKgnaE_2.boolean.opBoolean","INTERSECT",EDGE,{"derivedFrom":[makeQuery(id+"F3.boolean.opBoolean","MERGE",FACE,{"derivedFrom":[makeQuery(id+"F1.opExtrude","SWEPT_FACE",FACE,{"disambiguationData":[OSD([subQ1])]}),makeQuery(id+"F3.opExtrude","SWEPT_FACE",FACE,{"disambiguationData":[OSD([subQ1])]})]}),makeQuery(id+"F1ZY5U0QfWKgnaE_2.opExtrude","SWEPT_FACE",FACE,{"disambiguationData":[OSD([subQ0]),TDD([makeQuery(id+"FzWsDeid9OxCe4s_2.imprint","IMPRINT",EDGE,{"disambiguationData":[TD([[makeQuery(id+"FzWsDeid9OxCe4s_2.imprint","INTERSECT",VERTEX,{"derivedFrom":[subQ0,sQuery(id+"FzWsDeid9OxCe4s_2.wireOp",EDGE,"f3bd379a-a156-41d0-9f10-f2bbd5b9d83f.0")]}),-1.0]])],"derivedFrom":subQ0})])]})]});}
            var Q31;
            {var subQ0=sQuery(id+"F0.wireOp",EDGE,"E3");Q31=makeQuery(id+"F1ZY5U0QfWKgnaE_2.boolean.opBoolean","INTERSECT",EDGE,{"derivedFrom":[makeQuery(id+"F3.boolean.opBoolean","MERGE",FACE,{"derivedFrom":[makeQuery(id+"F1.opExtrude","SWEPT_FACE",FACE,{"disambiguationData":[OSD([subQ0])]}),makeQuery(id+"F3.opExtrude","SWEPT_FACE",FACE,{"disambiguationData":[OSD([subQ0])]})]}),makeQuery(id+"F1ZY5U0QfWKgnaE_2.opExtrude","SWEPT_FACE",FACE,{"disambiguationData":[OSD([sQuery(id+"FzWsDeid9OxCe4s_2.wireOp",EDGE,"f3bd379a-a156-41d0-9f10-f2bbd5b9d83f.0")])]})]});}
            var Q32;
            {var subQ0=sQuery(id+"FzWsDeid9OxCe4s_2.wireOp",EDGE,"DHWVtWLh-aHPT-YNDw-NuMh-FcVQlgM1t4xD");var subQ1=sQuery(id+"F0.wireOp",EDGE,"E3");Q32=makeQuery(id+"F1ZY5U0QfWKgnaE_2.boolean.opBoolean","INTERSECT",EDGE,{"derivedFrom":[makeQuery(id+"F3.boolean.opBoolean","MERGE",FACE,{"derivedFrom":[makeQuery(id+"F1.opExtrude","SWEPT_FACE",FACE,{"disambiguationData":[OSD([subQ1])]}),makeQuery(id+"F3.opExtrude","SWEPT_FACE",FACE,{"disambiguationData":[OSD([subQ1])]})]}),makeQuery(id+"F1ZY5U0QfWKgnaE_2.opExtrude","SWEPT_FACE",FACE,{"disambiguationData":[OSD([subQ0]),TDD([makeQuery(id+"FzWsDeid9OxCe4s_2.imprint","IMPRINT",EDGE,{"disambiguationData":[TD([[makeQuery(id+"FzWsDeid9OxCe4s_2.imprint","INTERSECT",VERTEX,{"derivedFrom":[subQ0,sQuery(id+"FzWsDeid9OxCe4s_2.wireOp",EDGE,"ddf2c67c-9696-4573-b7c7-edc6250c991e.0")]}),-1.0]])],"derivedFrom":subQ0})])]})]});}
            var Q33;
            {var subQ0=sQuery(id+"FzWsDeid9OxCe4s_2.wireOp",EDGE,"DHWVtWLh-aHPT-YNDw-NuMh-FcVQlgM1t4xD");var subQ1=sQuery(id+"F0.wireOp",EDGE,"E3");Q33=makeQuery(id+"F1ZY5U0QfWKgnaE_2.boolean.opBoolean","INTERSECT",EDGE,{"derivedFrom":[makeQuery(id+"F3.boolean.opBoolean","MERGE",FACE,{"derivedFrom":[makeQuery(id+"F1.opExtrude","SWEPT_FACE",FACE,{"disambiguationData":[OSD([subQ1])]}),makeQuery(id+"F3.opExtrude","SWEPT_FACE",FACE,{"disambiguationData":[OSD([subQ1])]})]}),makeQuery(id+"F1ZY5U0QfWKgnaE_2.opExtrude","SWEPT_FACE",FACE,{"disambiguationData":[OSD([subQ0]),TDD([makeQuery(id+"FzWsDeid9OxCe4s_2.imprint","IMPRINT",EDGE,{"disambiguationData":[TD([[makeQuery(id+"FzWsDeid9OxCe4s_2.imprint","INTERSECT",VERTEX,{"derivedFrom":[subQ0,sQuery(id+"FzWsDeid9OxCe4s_2.wireOp",EDGE,"f3bd379a-a156-41d0-9f10-f2bbd5b9d83f.0")]}),1.0]])],"derivedFrom":subQ0})])]})]});}
            var Q34;
            {var subQ0=sQuery(id+"F0.wireOp",EDGE,"E3");Q34=makeQuery(id+"F1ZY5U0QfWKgnaE_2.boolean.opBoolean","INTERSECT",EDGE,{"derivedFrom":[makeQuery(id+"F3.boolean.opBoolean","MERGE",FACE,{"derivedFrom":[makeQuery(id+"F1.opExtrude","SWEPT_FACE",FACE,{"disambiguationData":[OSD([subQ0])]}),makeQuery(id+"F3.opExtrude","SWEPT_FACE",FACE,{"disambiguationData":[OSD([subQ0])]})]}),makeQuery(id+"F1ZY5U0QfWKgnaE_2.opExtrude","SWEPT_FACE",FACE,{"disambiguationData":[OSD([sQuery(id+"FzWsDeid9OxCe4s_2.wireOp",EDGE,"52b8b0e7-0203-483f-8d4f-d96776e66651.0")])]})]});}
            var Q35;
            {var subQ0=sQuery(id+"FzWsDeid9OxCe4s_2.wireOp",EDGE,"DHWVtWLh-aHPT-YNDw-NuMh-FcVQlgM1t4xD");Q35=makeQuery(id+"F1ZY5U0QfWKgnaE_2.boolean.opBoolean","COPY",EDGE,{"derivedFrom":makeQuery(id+"F1ZY5U0QfWKgnaE_2.opExtrude","CAP_EDGE",EDGE,{"disambiguationData":[OSD([subQ0]),TDD([makeQuery(id+"FzWsDeid9OxCe4s_2.imprint","IMPRINT",EDGE,{"disambiguationData":[TD([[makeQuery(id+"FzWsDeid9OxCe4s_2.imprint","INTERSECT",VERTEX,{"derivedFrom":[subQ0,sQuery(id+"FzWsDeid9OxCe4s_2.wireOp",EDGE,"6cb0e26c-a951-431f-a703-2220c8751553.0")]}),1.0]])],"derivedFrom":subQ0})])],"isStart":true})});}
            var Q36;
            Q36=makeQuery(id+"F1ZY5U0QfWKgnaE_2.boolean.opBoolean","COPY",EDGE,{"derivedFrom":makeQuery(id+"F1ZY5U0QfWKgnaE_2.opExtrude","CAP_EDGE",EDGE,{"disambiguationData":[OSD([sQuery(id+"FzWsDeid9OxCe4s_2.wireOp",EDGE,"34e61975-36d3-4aa8-8ddd-237718441e8c.0")])],"isStart":true})});
            var Q37;
            {var subQ0=sQuery(id+"FzWsDeid9OxCe4s_2.wireOp",EDGE,"uo2K4ESE-ioYr-gu5B-DHa5-rfcAboMNfEFw");Q37=makeQuery(id+"F1ZY5U0QfWKgnaE_2.boolean.opBoolean","COPY",EDGE,{"derivedFrom":makeQuery(id+"F1ZY5U0QfWKgnaE_2.opExtrude","CAP_EDGE",EDGE,{"disambiguationData":[OSD([subQ0]),TDD([makeQuery(id+"FzWsDeid9OxCe4s_2.imprint","IMPRINT",EDGE,{"disambiguationData":[TD([[makeQuery(id+"FzWsDeid9OxCe4s_2.imprint","INTERSECT",VERTEX,{"derivedFrom":[subQ0,sQuery(id+"FzWsDeid9OxCe4s_2.wireOp",EDGE,"6cb0e26c-a951-431f-a703-2220c8751553.0")]}),-1.0]])],"derivedFrom":subQ0})])],"isStart":true})});}
            var Q38;
            Q38=makeQuery(id+"F1ZY5U0QfWKgnaE_2.boolean.opBoolean","COPY",EDGE,{"derivedFrom":makeQuery(id+"F1ZY5U0QfWKgnaE_2.opExtrude","CAP_EDGE",EDGE,{"disambiguationData":[OSD([sQuery(id+"FzWsDeid9OxCe4s_2.wireOp",EDGE,"af43ec8f-b541-4120-bac5-d7c26398eb1b.0")])],"isStart":true})});
            var Q39;
            {var subQ0=sQuery(id+"FzWsDeid9OxCe4s_2.wireOp",EDGE,"uo2K4ESE-ioYr-gu5B-DHa5-rfcAboMNfEFw");Q39=makeQuery(id+"F1ZY5U0QfWKgnaE_2.boolean.opBoolean","COPY",EDGE,{"derivedFrom":makeQuery(id+"F1ZY5U0QfWKgnaE_2.opExtrude","CAP_EDGE",EDGE,{"disambiguationData":[OSD([subQ0]),TDD([makeQuery(id+"FzWsDeid9OxCe4s_2.imprint","IMPRINT",EDGE,{"disambiguationData":[TD([[makeQuery(id+"FzWsDeid9OxCe4s_2.imprint","INTERSECT",VERTEX,{"derivedFrom":[subQ0,sQuery(id+"FzWsDeid9OxCe4s_2.wireOp",EDGE,"52b8b0e7-0203-483f-8d4f-d96776e66651.0")]}),1.0]])],"derivedFrom":subQ0})])],"isStart":true})});}
            var Q40;
            Q40=makeQuery(id+"F1ZY5U0QfWKgnaE_2.boolean.opBoolean","COPY",EDGE,{"derivedFrom":makeQuery(id+"F1ZY5U0QfWKgnaE_2.opExtrude","CAP_EDGE",EDGE,{"disambiguationData":[OSD([sQuery(id+"FzWsDeid9OxCe4s_2.wireOp",EDGE,"7e60bccf-3c07-404d-a5c6-af2364c06918.0")])],"isStart":true})});
            var Q41;
            {var subQ0=sQuery(id+"FzWsDeid9OxCe4s_2.wireOp",EDGE,"DHWVtWLh-aHPT-YNDw-NuMh-FcVQlgM1t4xD");Q41=makeQuery(id+"F1ZY5U0QfWKgnaE_2.boolean.opBoolean","COPY",EDGE,{"derivedFrom":makeQuery(id+"F1ZY5U0QfWKgnaE_2.opExtrude","CAP_EDGE",EDGE,{"disambiguationData":[OSD([subQ0]),TDD([makeQuery(id+"FzWsDeid9OxCe4s_2.imprint","IMPRINT",EDGE,{"disambiguationData":[TD([[makeQuery(id+"FzWsDeid9OxCe4s_2.imprint","INTERSECT",VERTEX,{"derivedFrom":[subQ0,sQuery(id+"FzWsDeid9OxCe4s_2.wireOp",EDGE,"52b8b0e7-0203-483f-8d4f-d96776e66651.0")]}),-1.0]])],"derivedFrom":subQ0})])],"isStart":true})});}
            var Q42;
            {var subQ0=sQuery(id+"FzWsDeid9OxCe4s_2.wireOp",EDGE,"DHWVtWLh-aHPT-YNDw-NuMh-FcVQlgM1t4xD");var subQ1=sQuery(id+"F0.wireOp",EDGE,"E1");Q42=makeQuery(id+"F1ZY5U0QfWKgnaE_2.boolean.opBoolean","INTERSECT",EDGE,{"derivedFrom":[makeQuery(id+"F3.boolean.opBoolean","MERGE",FACE,{"derivedFrom":[makeQuery(id+"F1.opExtrude","SWEPT_FACE",FACE,{"disambiguationData":[OSD([subQ1])]}),makeQuery(id+"F3.opExtrude","SWEPT_FACE",FACE,{"disambiguationData":[OSD([subQ1])]})]}),makeQuery(id+"F1ZY5U0QfWKgnaE_2.opExtrude","SWEPT_FACE",FACE,{"disambiguationData":[OSD([subQ0]),TDD([makeQuery(id+"FzWsDeid9OxCe4s_2.imprint","IMPRINT",EDGE,{"disambiguationData":[TD([[makeQuery(id+"FzWsDeid9OxCe4s_2.imprint","INTERSECT",VERTEX,{"derivedFrom":[subQ0,sQuery(id+"FzWsDeid9OxCe4s_2.wireOp",EDGE,"52b8b0e7-0203-483f-8d4f-d96776e66651.0")]}),-1.0]])],"derivedFrom":subQ0})])]})]});}
            var Q43;
            {var subQ0=sQuery(id+"F0.wireOp",EDGE,"E1");Q43=makeQuery(id+"F1ZY5U0QfWKgnaE_2.boolean.opBoolean","INTERSECT",EDGE,{"derivedFrom":[makeQuery(id+"F3.boolean.opBoolean","MERGE",FACE,{"derivedFrom":[makeQuery(id+"F1.opExtrude","SWEPT_FACE",FACE,{"disambiguationData":[OSD([subQ0])]}),makeQuery(id+"F3.opExtrude","SWEPT_FACE",FACE,{"disambiguationData":[OSD([subQ0])]})]}),makeQuery(id+"F1ZY5U0QfWKgnaE_2.opExtrude","SWEPT_FACE",FACE,{"disambiguationData":[OSD([sQuery(id+"FzWsDeid9OxCe4s_2.wireOp",EDGE,"0e0cef22-714b-4318-8aed-5ee99b345ba0.0")])]})]});}
            var Q44;
            Q44=makeQuery(id+"F1ZY5U0QfWKgnaE_2.boolean.opBoolean","COPY",EDGE,{"derivedFrom":makeQuery(id+"F1ZY5U0QfWKgnaE_2.opExtrude","CAP_EDGE",EDGE,{"disambiguationData":[OSD([sQuery(id+"FzWsDeid9OxCe4s_2.wireOp",EDGE,"0e0cef22-714b-4318-8aed-5ee99b345ba0.0")])],"isStart":true})});
            var Q45;
            {var subQ0=sQuery(id+"F0.wireOp",EDGE,"E1");Q45=makeQuery(id+"F1ZY5U0QfWKgnaE_2.boolean.opBoolean","INTERSECT",EDGE,{"derivedFrom":[makeQuery(id+"F3.boolean.opBoolean","MERGE",FACE,{"derivedFrom":[makeQuery(id+"F1.opExtrude","SWEPT_FACE",FACE,{"disambiguationData":[OSD([subQ0])]}),makeQuery(id+"F3.opExtrude","SWEPT_FACE",FACE,{"disambiguationData":[OSD([subQ0])]})]}),makeQuery(id+"F1ZY5U0QfWKgnaE_2.opExtrude","SWEPT_FACE",FACE,{"disambiguationData":[OSD([sQuery(id+"FzWsDeid9OxCe4s_2.wireOp",EDGE,"7e60bccf-3c07-404d-a5c6-af2364c06918.0")])]})]});}
            var Q46;
            {var subQ0=sQuery(id+"FzWsDeid9OxCe4s_2.wireOp",EDGE,"uo2K4ESE-ioYr-gu5B-DHa5-rfcAboMNfEFw");var subQ1=sQuery(id+"F0.wireOp",EDGE,"E1");Q46=makeQuery(id+"F1ZY5U0QfWKgnaE_2.boolean.opBoolean","INTERSECT",EDGE,{"derivedFrom":[makeQuery(id+"F3.boolean.opBoolean","MERGE",FACE,{"derivedFrom":[makeQuery(id+"F1.opExtrude","SWEPT_FACE",FACE,{"disambiguationData":[OSD([subQ1])]}),makeQuery(id+"F3.opExtrude","SWEPT_FACE",FACE,{"disambiguationData":[OSD([subQ1])]})]}),makeQuery(id+"F1ZY5U0QfWKgnaE_2.opExtrude","SWEPT_FACE",FACE,{"disambiguationData":[OSD([subQ0]),TDD([makeQuery(id+"FzWsDeid9OxCe4s_2.imprint","IMPRINT",EDGE,{"disambiguationData":[TD([[makeQuery(id+"FzWsDeid9OxCe4s_2.imprint","INTERSECT",VERTEX,{"derivedFrom":[subQ0,sQuery(id+"FzWsDeid9OxCe4s_2.wireOp",EDGE,"52b8b0e7-0203-483f-8d4f-d96776e66651.0")]}),1.0]])],"derivedFrom":subQ0})])]})]});}
            var Q47;
            {var subQ0=sQuery(id+"F0.wireOp",EDGE,"E1");Q47=makeQuery(id+"F1ZY5U0QfWKgnaE_2.boolean.opBoolean","INTERSECT",EDGE,{"derivedFrom":[makeQuery(id+"F3.boolean.opBoolean","MERGE",FACE,{"derivedFrom":[makeQuery(id+"F1.opExtrude","SWEPT_FACE",FACE,{"disambiguationData":[OSD([subQ0])]}),makeQuery(id+"F3.opExtrude","SWEPT_FACE",FACE,{"disambiguationData":[OSD([subQ0])]})]}),makeQuery(id+"F1ZY5U0QfWKgnaE_2.opExtrude","SWEPT_FACE",FACE,{"disambiguationData":[OSD([sQuery(id+"FzWsDeid9OxCe4s_2.wireOp",EDGE,"af43ec8f-b541-4120-bac5-d7c26398eb1b.0")])]})]});}
            var Q48;
            {var subQ0=sQuery(id+"F0.wireOp",EDGE,"E1");Q48=makeQuery(id+"F1ZY5U0QfWKgnaE_2.boolean.opBoolean","INTERSECT",EDGE,{"derivedFrom":[makeQuery(id+"F3.boolean.opBoolean","MERGE",FACE,{"derivedFrom":[makeQuery(id+"F1.opExtrude","SWEPT_FACE",FACE,{"disambiguationData":[OSD([subQ0])]}),makeQuery(id+"F3.opExtrude","SWEPT_FACE",FACE,{"disambiguationData":[OSD([subQ0])]})]}),makeQuery(id+"F1ZY5U0QfWKgnaE_2.opExtrude","SWEPT_FACE",FACE,{"disambiguationData":[OSD([sQuery(id+"FzWsDeid9OxCe4s_2.wireOp",EDGE,"34e61975-36d3-4aa8-8ddd-237718441e8c.0")])]})]});}
            var Q49;
            {var subQ0=sQuery(id+"FzWsDeid9OxCe4s_2.wireOp",EDGE,"DHWVtWLh-aHPT-YNDw-NuMh-FcVQlgM1t4xD");var subQ1=sQuery(id+"F0.wireOp",EDGE,"E1");Q49=makeQuery(id+"F1ZY5U0QfWKgnaE_2.boolean.opBoolean","INTERSECT",EDGE,{"derivedFrom":[makeQuery(id+"F3.boolean.opBoolean","MERGE",FACE,{"derivedFrom":[makeQuery(id+"F1.opExtrude","SWEPT_FACE",FACE,{"disambiguationData":[OSD([subQ1])]}),makeQuery(id+"F3.opExtrude","SWEPT_FACE",FACE,{"disambiguationData":[OSD([subQ1])]})]}),makeQuery(id+"F1ZY5U0QfWKgnaE_2.opExtrude","SWEPT_FACE",FACE,{"disambiguationData":[OSD([subQ0]),TDD([makeQuery(id+"FzWsDeid9OxCe4s_2.imprint","IMPRINT",EDGE,{"disambiguationData":[TD([[makeQuery(id+"FzWsDeid9OxCe4s_2.imprint","INTERSECT",VERTEX,{"derivedFrom":[subQ0,sQuery(id+"FzWsDeid9OxCe4s_2.wireOp",EDGE,"6cb0e26c-a951-431f-a703-2220c8751553.0")]}),1.0]])],"derivedFrom":subQ0})])]})]});}
            var Q50;
            {var subQ0=sQuery(id+"F0.wireOp",EDGE,"E4.1");Q50=makeQuery(id+"F1ZY5U0QfWKgnaE_2.boolean.opBoolean","INTERSECT",EDGE,{"derivedFrom":[makeQuery(id+"F2.boolean.opBoolean","MERGE",FACE,{"derivedFrom":[makeQuery(id+"F1.opExtrude","SWEPT_FACE",FACE,{"disambiguationData":[OSD([subQ0])]}),makeQuery(id+"F2.opExtrude","SWEPT_FACE",FACE,{"disambiguationData":[OSD([subQ0])]})]}),makeQuery(id+"F1ZY5U0QfWKgnaE_2.opExtrude","SWEPT_FACE",FACE,{"disambiguationData":[OSD([sQuery(id+"FzWsDeid9OxCe4s_2.wireOp",EDGE,"0e0cef22-714b-4318-8aed-5ee99b345ba0.0")])]})]});}
            var Q51;
            {var subQ0=sQuery(id+"F0.wireOp",EDGE,"E4.1");Q51=makeQuery(id+"F1ZY5U0QfWKgnaE_2.boolean.opBoolean","INTERSECT",EDGE,{"derivedFrom":[makeQuery(id+"F2.boolean.opBoolean","MERGE",FACE,{"derivedFrom":[makeQuery(id+"F1.opExtrude","SWEPT_FACE",FACE,{"disambiguationData":[OSD([subQ0])]}),makeQuery(id+"F2.opExtrude","SWEPT_FACE",FACE,{"disambiguationData":[OSD([subQ0])]})]}),makeQuery(id+"F1ZY5U0QfWKgnaE_2.opExtrude","SWEPT_FACE",FACE,{"disambiguationData":[OSD([sQuery(id+"FzWsDeid9OxCe4s_2.wireOp",EDGE,"7e60bccf-3c07-404d-a5c6-af2364c06918.0")])]})]});}
            var Q52;
            {var subQ0=sQuery(id+"FzWsDeid9OxCe4s_2.wireOp",EDGE,"DHWVtWLh-aHPT-YNDw-NuMh-FcVQlgM1t4xD");var subQ1=sQuery(id+"F0.wireOp",EDGE,"E4.1");Q52=makeQuery(id+"F1ZY5U0QfWKgnaE_2.boolean.opBoolean","INTERSECT",EDGE,{"derivedFrom":[makeQuery(id+"F2.boolean.opBoolean","MERGE",FACE,{"derivedFrom":[makeQuery(id+"F1.opExtrude","SWEPT_FACE",FACE,{"disambiguationData":[OSD([subQ1])]}),makeQuery(id+"F2.opExtrude","SWEPT_FACE",FACE,{"disambiguationData":[OSD([subQ1])]})]}),makeQuery(id+"F1ZY5U0QfWKgnaE_2.opExtrude","SWEPT_FACE",FACE,{"disambiguationData":[OSD([subQ0]),TDD([makeQuery(id+"FzWsDeid9OxCe4s_2.imprint","IMPRINT",EDGE,{"disambiguationData":[TD([[makeQuery(id+"FzWsDeid9OxCe4s_2.imprint","INTERSECT",VERTEX,{"derivedFrom":[subQ0,sQuery(id+"FzWsDeid9OxCe4s_2.wireOp",EDGE,"52b8b0e7-0203-483f-8d4f-d96776e66651.0")]}),-1.0]])],"derivedFrom":subQ0})])]})]});}
            var Q53;
            {var subQ0=sQuery(id+"FzWsDeid9OxCe4s_2.wireOp",EDGE,"uo2K4ESE-ioYr-gu5B-DHa5-rfcAboMNfEFw");var subQ1=sQuery(id+"F0.wireOp",EDGE,"E4.1");Q53=makeQuery(id+"F1ZY5U0QfWKgnaE_2.boolean.opBoolean","INTERSECT",EDGE,{"derivedFrom":[makeQuery(id+"F2.boolean.opBoolean","MERGE",FACE,{"derivedFrom":[makeQuery(id+"F1.opExtrude","SWEPT_FACE",FACE,{"disambiguationData":[OSD([subQ1])]}),makeQuery(id+"F2.opExtrude","SWEPT_FACE",FACE,{"disambiguationData":[OSD([subQ1])]})]}),makeQuery(id+"F1ZY5U0QfWKgnaE_2.opExtrude","SWEPT_FACE",FACE,{"disambiguationData":[OSD([subQ0]),TDD([makeQuery(id+"FzWsDeid9OxCe4s_2.imprint","IMPRINT",EDGE,{"disambiguationData":[TD([[makeQuery(id+"FzWsDeid9OxCe4s_2.imprint","INTERSECT",VERTEX,{"derivedFrom":[subQ0,sQuery(id+"FzWsDeid9OxCe4s_2.wireOp",EDGE,"52b8b0e7-0203-483f-8d4f-d96776e66651.0")]}),1.0]])],"derivedFrom":subQ0})])]})]});}
            var Q54;
            {var subQ0=sQuery(id+"FzWsDeid9OxCe4s_2.wireOp",EDGE,"DHWVtWLh-aHPT-YNDw-NuMh-FcVQlgM1t4xD");var subQ1=sQuery(id+"F0.wireOp",EDGE,"E3");Q54=makeQuery(id+"F1ZY5U0QfWKgnaE_2.boolean.opBoolean","INTERSECT",EDGE,{"derivedFrom":[makeQuery(id+"F3.boolean.opBoolean","MERGE",FACE,{"derivedFrom":[makeQuery(id+"F1.opExtrude","SWEPT_FACE",FACE,{"disambiguationData":[OSD([subQ1])]}),makeQuery(id+"F3.opExtrude","SWEPT_FACE",FACE,{"disambiguationData":[OSD([subQ1])]})]}),makeQuery(id+"F1ZY5U0QfWKgnaE_2.opExtrude","SWEPT_FACE",FACE,{"disambiguationData":[OSD([subQ0]),TDD([makeQuery(id+"FzWsDeid9OxCe4s_2.imprint","IMPRINT",EDGE,{"disambiguationData":[TD([[makeQuery(id+"FzWsDeid9OxCe4s_2.imprint","INTERSECT",VERTEX,{"derivedFrom":[subQ0,sQuery(id+"FzWsDeid9OxCe4s_2.wireOp",EDGE,"52b8b0e7-0203-483f-8d4f-d96776e66651.0")]}),-1.0]])],"derivedFrom":subQ0})])]})]});}
            var Q55;
            {var subQ0=sQuery(id+"F0.wireOp",EDGE,"E3");Q55=makeQuery(id+"F1ZY5U0QfWKgnaE_2.boolean.opBoolean","INTERSECT",EDGE,{"derivedFrom":[makeQuery(id+"F3.boolean.opBoolean","MERGE",FACE,{"derivedFrom":[makeQuery(id+"F1.opExtrude","SWEPT_FACE",FACE,{"disambiguationData":[OSD([subQ0])]}),makeQuery(id+"F3.opExtrude","SWEPT_FACE",FACE,{"disambiguationData":[OSD([subQ0])]})]}),makeQuery(id+"F1ZY5U0QfWKgnaE_2.opExtrude","SWEPT_FACE",FACE,{"disambiguationData":[OSD([sQuery(id+"FzWsDeid9OxCe4s_2.wireOp",EDGE,"7e60bccf-3c07-404d-a5c6-af2364c06918.0")])]})]});}
            var Q56;
            {var subQ0=sQuery(id+"F0.wireOp",EDGE,"E3");Q56=makeQuery(id+"F1ZY5U0QfWKgnaE_2.boolean.opBoolean","INTERSECT",EDGE,{"derivedFrom":[makeQuery(id+"F3.boolean.opBoolean","MERGE",FACE,{"derivedFrom":[makeQuery(id+"F1.opExtrude","SWEPT_FACE",FACE,{"disambiguationData":[OSD([subQ0])]}),makeQuery(id+"F3.opExtrude","SWEPT_FACE",FACE,{"disambiguationData":[OSD([subQ0])]})]}),makeQuery(id+"F1ZY5U0QfWKgnaE_2.opExtrude","SWEPT_FACE",FACE,{"disambiguationData":[OSD([sQuery(id+"FzWsDeid9OxCe4s_2.wireOp",EDGE,"af43ec8f-b541-4120-bac5-d7c26398eb1b.0")])]})]});}
            var Q57;
            {var subQ0=sQuery(id+"F0.wireOp",EDGE,"E4.1");Q57=makeQuery(id+"F1ZY5U0QfWKgnaE_2.boolean.opBoolean","INTERSECT",EDGE,{"derivedFrom":[makeQuery(id+"F2.boolean.opBoolean","MERGE",FACE,{"derivedFrom":[makeQuery(id+"F1.opExtrude","SWEPT_FACE",FACE,{"disambiguationData":[OSD([subQ0])]}),makeQuery(id+"F2.opExtrude","SWEPT_FACE",FACE,{"disambiguationData":[OSD([subQ0])]})]}),makeQuery(id+"F1ZY5U0QfWKgnaE_2.opExtrude","SWEPT_FACE",FACE,{"disambiguationData":[OSD([sQuery(id+"FzWsDeid9OxCe4s_2.wireOp",EDGE,"af43ec8f-b541-4120-bac5-d7c26398eb1b.0")])]})]});}
            var Q58;
            {var subQ0=sQuery(id+"FzWsDeid9OxCe4s_2.wireOp",EDGE,"DHWVtWLh-aHPT-YNDw-NuMh-FcVQlgM1t4xD");var subQ1=sQuery(id+"F0.wireOp",EDGE,"E4.1");Q58=makeQuery(id+"F1ZY5U0QfWKgnaE_2.boolean.opBoolean","INTERSECT",EDGE,{"derivedFrom":[makeQuery(id+"F2.boolean.opBoolean","MERGE",FACE,{"derivedFrom":[makeQuery(id+"F1.opExtrude","SWEPT_FACE",FACE,{"disambiguationData":[OSD([subQ1])]}),makeQuery(id+"F2.opExtrude","SWEPT_FACE",FACE,{"disambiguationData":[OSD([subQ1])]})]}),makeQuery(id+"F1ZY5U0QfWKgnaE_2.opExtrude","SWEPT_FACE",FACE,{"disambiguationData":[OSD([subQ0]),TDD([makeQuery(id+"FzWsDeid9OxCe4s_2.imprint","IMPRINT",EDGE,{"disambiguationData":[TD([[makeQuery(id+"FzWsDeid9OxCe4s_2.imprint","INTERSECT",VERTEX,{"derivedFrom":[subQ0,sQuery(id+"FzWsDeid9OxCe4s_2.wireOp",EDGE,"6cb0e26c-a951-431f-a703-2220c8751553.0")]}),1.0]])],"derivedFrom":subQ0})])]})]});}
            var Q59;
            {var subQ0=sQuery(id+"F0.wireOp",EDGE,"E4.1");Q59=makeQuery(id+"F1ZY5U0QfWKgnaE_2.boolean.opBoolean","INTERSECT",EDGE,{"derivedFrom":[makeQuery(id+"F2.boolean.opBoolean","MERGE",FACE,{"derivedFrom":[makeQuery(id+"F1.opExtrude","SWEPT_FACE",FACE,{"disambiguationData":[OSD([subQ0])]}),makeQuery(id+"F2.opExtrude","SWEPT_FACE",FACE,{"disambiguationData":[OSD([subQ0])]})]}),makeQuery(id+"F1ZY5U0QfWKgnaE_2.opExtrude","SWEPT_FACE",FACE,{"disambiguationData":[OSD([sQuery(id+"FzWsDeid9OxCe4s_2.wireOp",EDGE,"34e61975-36d3-4aa8-8ddd-237718441e8c.0")])]})]});}
            var Q60;
            {var subQ0=sQuery(id+"FzWsDeid9OxCe4s_2.wireOp",EDGE,"uo2K4ESE-ioYr-gu5B-DHa5-rfcAboMNfEFw");var subQ1=sQuery(id+"F0.wireOp",EDGE,"E4.1");Q60=makeQuery(id+"F1ZY5U0QfWKgnaE_2.boolean.opBoolean","INTERSECT",EDGE,{"derivedFrom":[makeQuery(id+"F2.boolean.opBoolean","MERGE",FACE,{"derivedFrom":[makeQuery(id+"F1.opExtrude","SWEPT_FACE",FACE,{"disambiguationData":[OSD([subQ1])]}),makeQuery(id+"F2.opExtrude","SWEPT_FACE",FACE,{"disambiguationData":[OSD([subQ1])]})]}),makeQuery(id+"F1ZY5U0QfWKgnaE_2.opExtrude","SWEPT_FACE",FACE,{"disambiguationData":[OSD([subQ0]),TDD([makeQuery(id+"FzWsDeid9OxCe4s_2.imprint","IMPRINT",EDGE,{"disambiguationData":[TD([[makeQuery(id+"FzWsDeid9OxCe4s_2.imprint","INTERSECT",VERTEX,{"derivedFrom":[subQ0,sQuery(id+"FzWsDeid9OxCe4s_2.wireOp",EDGE,"6cb0e26c-a951-431f-a703-2220c8751553.0")]}),-1.0]])],"derivedFrom":subQ0})])]})]});}
            var Q61;
            {var subQ0=sQuery(id+"FzWsDeid9OxCe4s_2.wireOp",EDGE,"DHWVtWLh-aHPT-YNDw-NuMh-FcVQlgM1t4xD");var subQ1=sQuery(id+"F0.wireOp",EDGE,"E3");Q61=makeQuery(id+"F1ZY5U0QfWKgnaE_2.boolean.opBoolean","INTERSECT",EDGE,{"derivedFrom":[makeQuery(id+"F3.boolean.opBoolean","MERGE",FACE,{"derivedFrom":[makeQuery(id+"F1.opExtrude","SWEPT_FACE",FACE,{"disambiguationData":[OSD([subQ1])]}),makeQuery(id+"F3.opExtrude","SWEPT_FACE",FACE,{"disambiguationData":[OSD([subQ1])]})]}),makeQuery(id+"F1ZY5U0QfWKgnaE_2.opExtrude","SWEPT_FACE",FACE,{"disambiguationData":[OSD([subQ0]),TDD([makeQuery(id+"FzWsDeid9OxCe4s_2.imprint","IMPRINT",EDGE,{"disambiguationData":[TD([[makeQuery(id+"FzWsDeid9OxCe4s_2.imprint","INTERSECT",VERTEX,{"derivedFrom":[subQ0,sQuery(id+"FzWsDeid9OxCe4s_2.wireOp",EDGE,"6cb0e26c-a951-431f-a703-2220c8751553.0")]}),1.0]])],"derivedFrom":subQ0})])]})]});}
            var Q62;
            {var subQ0=sQuery(id+"FzWsDeid9OxCe4s_2.wireOp",EDGE,"uo2K4ESE-ioYr-gu5B-DHa5-rfcAboMNfEFw");var subQ1=sQuery(id+"F0.wireOp",EDGE,"E3");Q62=makeQuery(id+"F1ZY5U0QfWKgnaE_2.boolean.opBoolean","INTERSECT",EDGE,{"derivedFrom":[makeQuery(id+"F3.boolean.opBoolean","MERGE",FACE,{"derivedFrom":[makeQuery(id+"F1.opExtrude","SWEPT_FACE",FACE,{"disambiguationData":[OSD([subQ1])]}),makeQuery(id+"F3.opExtrude","SWEPT_FACE",FACE,{"disambiguationData":[OSD([subQ1])]})]}),makeQuery(id+"F1ZY5U0QfWKgnaE_2.opExtrude","SWEPT_FACE",FACE,{"disambiguationData":[OSD([subQ0]),TDD([makeQuery(id+"FzWsDeid9OxCe4s_2.imprint","IMPRINT",EDGE,{"disambiguationData":[TD([[makeQuery(id+"FzWsDeid9OxCe4s_2.imprint","INTERSECT",VERTEX,{"derivedFrom":[subQ0,sQuery(id+"FzWsDeid9OxCe4s_2.wireOp",EDGE,"6cb0e26c-a951-431f-a703-2220c8751553.0")]}),-1.0]])],"derivedFrom":subQ0})])]})]});}
            var Q63;
            {var subQ0=sQuery(id+"F0.wireOp",EDGE,"E3");Q63=makeQuery(id+"F1ZY5U0QfWKgnaE_2.boolean.opBoolean","INTERSECT",EDGE,{"derivedFrom":[makeQuery(id+"F3.boolean.opBoolean","MERGE",FACE,{"derivedFrom":[makeQuery(id+"F1.opExtrude","SWEPT_FACE",FACE,{"disambiguationData":[OSD([subQ0])]}),makeQuery(id+"F3.opExtrude","SWEPT_FACE",FACE,{"disambiguationData":[OSD([subQ0])]})]}),makeQuery(id+"F1ZY5U0QfWKgnaE_2.opExtrude","SWEPT_FACE",FACE,{"disambiguationData":[OSD([sQuery(id+"FzWsDeid9OxCe4s_2.wireOp",EDGE,"34e61975-36d3-4aa8-8ddd-237718441e8c.0")])]})]});}
            var Q64;
            {var subQ0=sQuery(id+"F0.wireOp",EDGE,"E3");Q64=makeQuery(id+"F1ZY5U0QfWKgnaE_2.boolean.opBoolean","INTERSECT",EDGE,{"derivedFrom":[makeQuery(id+"F3.boolean.opBoolean","MERGE",FACE,{"derivedFrom":[makeQuery(id+"F1.opExtrude","SWEPT_FACE",FACE,{"disambiguationData":[OSD([subQ0])]}),makeQuery(id+"F3.opExtrude","SWEPT_FACE",FACE,{"disambiguationData":[OSD([subQ0])]})]}),makeQuery(id+"F1ZY5U0QfWKgnaE_2.opExtrude","SWEPT_FACE",FACE,{"disambiguationData":[OSD([sQuery(id+"FzWsDeid9OxCe4s_2.wireOp",EDGE,"0e0cef22-714b-4318-8aed-5ee99b345ba0.0")])]})]});}
            var Q65;
            {var subQ0=sQuery(id+"FzWsDeid9OxCe4s_2.wireOp",EDGE,"uo2K4ESE-ioYr-gu5B-DHa5-rfcAboMNfEFw");var subQ1=sQuery(id+"F0.wireOp",EDGE,"E3");Q65=makeQuery(id+"F1ZY5U0QfWKgnaE_2.boolean.opBoolean","INTERSECT",EDGE,{"derivedFrom":[makeQuery(id+"F3.boolean.opBoolean","MERGE",FACE,{"derivedFrom":[makeQuery(id+"F1.opExtrude","SWEPT_FACE",FACE,{"disambiguationData":[OSD([subQ1])]}),makeQuery(id+"F3.opExtrude","SWEPT_FACE",FACE,{"disambiguationData":[OSD([subQ1])]})]}),makeQuery(id+"F1ZY5U0QfWKgnaE_2.opExtrude","SWEPT_FACE",FACE,{"disambiguationData":[OSD([subQ0]),TDD([makeQuery(id+"FzWsDeid9OxCe4s_2.imprint","IMPRINT",EDGE,{"disambiguationData":[TD([[makeQuery(id+"FzWsDeid9OxCe4s_2.imprint","INTERSECT",VERTEX,{"derivedFrom":[subQ0,sQuery(id+"FzWsDeid9OxCe4s_2.wireOp",EDGE,"52b8b0e7-0203-483f-8d4f-d96776e66651.0")]}),1.0]])],"derivedFrom":subQ0})])]})]});}
            fillet(context, id + "F5", {"entities" : qUnion([Q0, Q1, Q2, Q3, Q4, Q5, Q6, Q7, Q8, Q9, Q10, Q11, Q12, Q13, Q14, Q15, Q16, Q17, Q18, Q19, Q20, Q21, Q22, Q23, Q24, Q25, Q26, Q27, Q28, Q29, Q30, Q31, Q32, Q33, Q34, Q35, Q36, Q37, Q38, Q39, Q40, Q41, Q42, Q43, Q44, Q45, Q46, Q47, Q48, Q49, Q50, Q51, Q52, Q53, Q54, Q55, Q56, Q57, Q58, Q59, Q60, Q61, Q62, Q63, Q64, Q65]), "radius" : 1 * mm, "tangentPropagation" : true, "allowEdgeOverflow" : false});
        }
        {
            var Q0;
            Q0=qCreatedBy(makeId("Front.planeOp"),FACE);
            var sketch = newSketch(context, id + "F6", { "sketchPlane" : qUnion([Q0])});
            skLineSegment(sketch, "E39", {"start": v(1.01, 0) * mm, "end": v(1.01, 32.7) * mm});
            skLineSegment(sketch, "E40", {"start": v(1.01, 32.7) * mm, "end": v(-101.79, 32.7) * mm});
            skLineSegment(sketch, "E41", {"start": v(-101.79, 32.7) * mm, "end": v(-101.79, 0) * mm});
            skLineSegment(sketch, "E42", {"start": v(-101.79, 0) * mm, "end": v(1.01, 0) * mm});
            skLineSegment(sketch, "E43", {"start": v(1.01, 32.7) * mm, "end": v(-13.49, 32.7) * mm});
            skLineSegment(sketch, "E44", {"start": v(1.01, 32.7) * mm, "end": v(1.01, 18.2) * mm});
            skCircle(sketch, "E45", {"center": v(-6.24, 25.45) * mm, "radius": 6 * mm});
            skPoint(sketch, "E45.centerSnap0", {"position": v(-6.24, 32.7) * mm});
            skPoint(sketch, "E45.centerSnap1", {"position": v(1.01, 25.45) * mm});
            skLineSegment(sketch, "E46", {"start": v(-101.79, 32.7) * mm, "end": v(-101.79, 24.7) * mm});
            skLineSegment(sketch, "E47", {"start": v(-101.79, 24.7) * mm, "end": v(-93.29, 24.7) * mm});
            skLineSegment(sketch, "E48", {"start": v(-93.29, 24.7) * mm, "end": v(-93.29, 28.2) * mm});
            skLineSegment(sketch, "E49", {"start": v(-93.29, 28.2) * mm, "end": v(-73.29, 28.2) * mm});
            skLineSegment(sketch, "E50", {"start": v(-73.29, 28.2) * mm, "end": v(-73.29, 24.7) * mm});
            skLineSegment(sketch, "E51", {"start": v(-73.29, 24.7) * mm, "end": v(-93.29, 24.7) * mm});
            skLineSegment(sketch, "E52", {"start": v(-73.29, 28.2) * mm, "end": v(-76.79, 28.2) * mm});
            skLineSegment(sketch, "E53", {"start": v(-93.29, 28.2) * mm, "end": v(-89.79, 28.2) * mm});
            skLineSegment(sketch, "E54.0", {"start": v(-94.79, 29.7) * mm, "end": v(-71.79, 29.7) * mm});
            skLineSegment(sketch, "E54.1", {"start": v(-94.79, 23.2) * mm, "end": v(-94.79, 29.7) * mm});
            skLineSegment(sketch, "E54.2", {"start": v(-71.79, 23.2) * mm, "end": v(-94.79, 23.2) * mm});
            skLineSegment(sketch, "E54.3", {"start": v(-71.79, 29.7) * mm, "end": v(-71.79, 23.2) * mm});
            skLineSegment(sketch, "E55", {"start": v(1.01, 32.7) * mm, "end": v(1.01, 16.7) * mm});
            skLineSegment(sketch, "E56", {"start": v(1.01, 16.7) * mm, "end": v(-22.49, 16.7) * mm});
            skLineSegment(sketch, "E57", {"start": v(-22.49, 16.7) * mm, "end": v(-22.49, 23.7) * mm});
            skLineSegment(sketch, "E58", {"start": v(-22.49, 23.7) * mm, "end": v(-14.99, 23.7) * mm});
            skLineSegment(sketch, "E59", {"start": v(-14.99, 23.7) * mm, "end": v(-14.99, 16.7) * mm});
            skLineSegment(sketch, "E60.0", {"start": v(-9.63, 30.7) * mm, "end": v(-13.49, 30.7) * mm});
            skLineSegment(sketch, "E61.0", {"start": v(-0.99, 3) * mm, "end": v(-0.99, 22.06) * mm});
            skLineSegment(sketch, "E62", {"start": v(1.01, 0) * mm, "end": v(-53.99, 0) * mm});
            skLineSegment(sketch, "E63.0", {"start": v(-0.99, 3) * mm, "end": v(-53.99, 3) * mm});
            skLineSegment(sketch, "E64", {"start": v(-13.49, 32.7) * mm, "end": v(-13.49, 30.7) * mm});
            skLineSegment(sketch, "E65", {"start": v(-53.99, 3) * mm, "end": v(-53.99, 0) * mm});
            skLineSegment(sketch, "E66", {"start": v(-101.79, 32.7) * mm, "end": v(-96.79, 32.7) * mm});
            skLineSegment(sketch, "E67", {"start": v(-96.79, 32.7) * mm, "end": v(-96.79, 20.7) * mm});
            skLineSegment(sketch, "E68", {"start": v(-96.79, 20.7) * mm, "end": v(-101.79, 20.7) * mm});
            skCircle(sketch, "E69.0", {"center": v(-6.24, 25.45) * mm, "radius": 6.25 * mm});
            skSolve(sketch);
        }
        {
            var Q0;
            {var subQ2=sQuery(id+"F6.wireOp",EDGE,"E48");Q0=makeQuery(id+"F6.imprint","IMPRINT",FACE,{"disambiguationData":[TD([[makeQuery(id+"F6.imprint","IMPRINT",EDGE,{"derivedFrom":subQ2}),1.0]])]});}
            var Q1;
            Q1=makeQuery(id+"F6.imprint","IMPRINT",FACE,{"disambiguationData":[TD([[makeQuery(id+"F6.imprint","IMPRINT",EDGE,{"derivedFrom":sQuery(id+"F6.wireOp",EDGE,"E40")}),1.0]])]});
            var Q2;
            {var subQ4=sQuery(id+"F6.wireOp",EDGE,"E39");Q2=makeQuery(id+"F6.imprint","IMPRINT",FACE,{"disambiguationData":[TD([[makeQuery(id+"F6.imprint","IMPRINT",EDGE,{"derivedFrom":subQ4}),1.0]])]});}
            var Q3;
            {var subQ6=sQuery(id+"F6.wireOp",EDGE,"E43");Q3=makeQuery(id+"F6.imprint","IMPRINT",FACE,{"disambiguationData":[TD([[makeQuery(id+"F6.imprint","IMPRINT",EDGE,{"derivedFrom":subQ6}),1.0]])]});}
            var Q4;
            {var subQ0=sQuery(id+"F6.wireOp",EDGE,"E46");Q4=makeQuery(id+"F6.imprint","IMPRINT",FACE,{"disambiguationData":[TD([[makeQuery(id+"F6.imprint","IMPRINT",EDGE,{"derivedFrom":subQ0}),1.0]])]});}
            var Q5;
            {var subQ3=sQuery(id+"F6.wireOp",EDGE,"E68");Q5=makeQuery(id+"F6.imprint","IMPRINT",FACE,{"disambiguationData":[TD([[makeQuery(id+"F6.imprint","IMPRINT",EDGE,{"derivedFrom":subQ3}),-1.0]])]});}
            extrude(context, id + "F7", {"entities" : qUnion([Q0, Q1, Q2, Q3, Q4, Q5]), "oppositeDirection" : true, "depth" : 3 * mm});
        }
        {
            var Q0;
            {var subQ2=sQuery(id+"F6.wireOp",EDGE,"E48");Q0=makeQuery(id+"F6.imprint","IMPRINT",FACE,{"disambiguationData":[TD([[makeQuery(id+"F6.imprint","IMPRINT",EDGE,{"derivedFrom":subQ2}),1.0]])]});}
            var Q1;
            Q1=makeQuery(id+"F6.imprint","IMPRINT",FACE,{"disambiguationData":[TD([[makeQuery(id+"F6.imprint","IMPRINT",EDGE,{"derivedFrom":sQuery(id+"F6.wireOp",EDGE,"E49")}),-1.0]])]});
            extrude(context, id + "F8", {"entities" : qUnion([Q0, Q1]), "operationType" : NewBodyOperationType.REMOVE, "oppositeDirection" : true, "depth" : 2 * mm});
        }
        {
            var Q0;
            {var subQ4=sQuery(id+"F6.wireOp",EDGE,"E39");Q0=makeQuery(id+"F6.imprint","IMPRINT",FACE,{"disambiguationData":[TD([[makeQuery(id+"F6.imprint","IMPRINT",EDGE,{"derivedFrom":subQ4}),1.0]])]});}
            var Q1;
            {var subQ6=sQuery(id+"F6.wireOp",EDGE,"E43");Q1=makeQuery(id+"F6.imprint","IMPRINT",FACE,{"disambiguationData":[TD([[makeQuery(id+"F6.imprint","IMPRINT",EDGE,{"derivedFrom":subQ6}),1.0]])]});}
            var Q2;
            {var subQ0=sQuery(id+"F6.wireOp",EDGE,"E46");Q2=makeQuery(id+"F6.imprint","IMPRINT",FACE,{"disambiguationData":[TD([[makeQuery(id+"F6.imprint","IMPRINT",EDGE,{"derivedFrom":subQ0}),1.0]])]});}
            var Q3;
            {var subQ3=sQuery(id+"F6.wireOp",EDGE,"E68");Q3=makeQuery(id+"F6.imprint","IMPRINT",FACE,{"disambiguationData":[TD([[makeQuery(id+"F6.imprint","IMPRINT",EDGE,{"derivedFrom":subQ3}),-1.0]])]});}
            extrude(context, id + "F9", {"entities" : qUnion([Q0, Q1, Q2, Q3]), "operationType" : NewBodyOperationType.ADD, "depth" : 2 * mm});
        }
        {
            var Q0;
            Q0=makeQuery(id+"F7.opExtrude","CAP_EDGE",EDGE,{"disambiguationData":[OSD([sQuery(id+"F6.wireOp",EDGE,"E41"),sQuery(id+"F6.wireOp",EDGE,"E46")])],"isStart":false});
            var Q1;
            Q1=makeQuery(id+"F7.opExtrude","CAP_EDGE",EDGE,{"disambiguationData":[OSD([sQuery(id+"F6.wireOp",EDGE,"E40"),sQuery(id+"F6.wireOp",EDGE,"E43")])],"isStart":false});
            var Q2;
            Q2=makeQuery(id+"F7.opExtrude","CAP_EDGE",EDGE,{"disambiguationData":[OSD([sQuery(id+"F6.wireOp",EDGE,"E39"),sQuery(id+"F6.wireOp",EDGE,"E55")])],"isStart":false});
            var Q3;
            Q3=makeQuery(id+"F7.opExtrude","CAP_EDGE",EDGE,{"disambiguationData":[OSD([sQuery(id+"F6.wireOp",EDGE,"E42")])],"isStart":false});
            var Q4;
            Q4=makeQuery(id+"F7.opExtrude","CAP_FACE",FACE,{"disambiguationData":[OSD([sQuery(id+"F6.wireOp",EDGE,"E39"),sQuery(id+"F6.wireOp",EDGE,"E40"),sQuery(id+"F6.wireOp",EDGE,"E41"),sQuery(id+"F6.wireOp",EDGE,"E42"),sQuery(id+"F6.wireOp",EDGE,"E43"),sQuery(id+"F6.wireOp",EDGE,"E45"),sQuery(id+"F6.wireOp",EDGE,"E46"),sQuery(id+"F6.wireOp",EDGE,"E48"),sQuery(id+"F6.wireOp",EDGE,"E50"),sQuery(id+"F6.wireOp",EDGE,"E51"),sQuery(id+"F6.wireOp",EDGE,"E52"),sQuery(id+"F6.wireOp",EDGE,"1LZiOuj2-O9iR-LT3f-GXDr-0R7zgSD0xn0j"),sQuery(id+"F6.wireOp",EDGE,"E53"),sQuery(id+"F6.wireOp",EDGE,"scusgCRg-7Ny1-5VAw-mZsh-GK8Lg82yCSxJ"),sQuery(id+"F6.wireOp",EDGE,"E55"),sQuery(id+"F6.wireOp",EDGE,"E56"),sQuery(id+"F6.wireOp",EDGE,"E57"),sQuery(id+"F6.wireOp",EDGE,"E58"),sQuery(id+"F6.wireOp",EDGE,"E59")])],"isStart":false});
            var Q5;
            Q5=makeQuery(id+"F7.opExtrude","CAP_EDGE",EDGE,{"disambiguationData":[OSD([sQuery(id+"F6.wireOp",EDGE,"E41"),sQuery(id+"F6.wireOp",EDGE,"E46")])],"isStart":true});
            var Q6;
            Q6=makeQuery(id+"F7.opExtrude","SWEPT_EDGE",EDGE,{"disambiguationData":[OSD([sQuery(id+"F6.wireOp",EDGE,"E40"),sQuery(id+"F6.wireOp",EDGE,"E46")])]});
            var Q7;
            Q7=makeQuery(id+"F7.opExtrude","CAP_EDGE",EDGE,{"disambiguationData":[OSD([sQuery(id+"F6.wireOp",EDGE,"E40"),sQuery(id+"F6.wireOp",EDGE,"E43")])],"isStart":true});
            var Q8;
            Q8=makeQuery(id+"F7.opExtrude","CAP_EDGE",EDGE,{"disambiguationData":[OSD([sQuery(id+"F6.wireOp",EDGE,"E42")])],"isStart":true});
            var Q9;
            Q9=makeQuery(id+"F7.opExtrude","CAP_EDGE",EDGE,{"disambiguationData":[OSD([sQuery(id+"F6.wireOp",EDGE,"E39"),sQuery(id+"F6.wireOp",EDGE,"E55")])],"isStart":true});
            var Q10;
            Q10=makeQuery(id+"F7.opExtrude","SWEPT_EDGE",EDGE,{"disambiguationData":[OSD([sQuery(id+"F6.wireOp",EDGE,"E43"),sQuery(id+"F6.wireOp",EDGE,"E55")])]});
            var Q11;
            Q11=makeQuery(id+"F7.opExtrude","SWEPT_EDGE",EDGE,{"disambiguationData":[OSD([sQuery(id+"F6.wireOp",EDGE,"E39"),sQuery(id+"F6.wireOp",EDGE,"E42")])]});
            var Q12;
            Q12=makeQuery(id+"F7.opExtrude","SWEPT_EDGE",EDGE,{"disambiguationData":[OSD([sQuery(id+"F6.wireOp",EDGE,"E41"),sQuery(id+"F6.wireOp",EDGE,"E42")])]});
            var Q13;
            Q13=makeQuery(id+"F7.opExtrude","CAP_EDGE",EDGE,{"disambiguationData":[OSD([sQuery(id+"F6.wireOp",EDGE,"E58")])],"isStart":true});
            var Q14;
            Q14=makeQuery(id+"F7.opExtrude","CAP_EDGE",EDGE,{"disambiguationData":[OSD([sQuery(id+"F6.wireOp",EDGE,"E57")])],"isStart":true});
            var Q15;
            Q15=makeQuery(id+"F7.opExtrude","CAP_EDGE",EDGE,{"disambiguationData":[OSD([sQuery(id+"F6.wireOp",EDGE,"E45")])],"isStart":true});
            var Q16;
            Q16=makeQuery(id+"F8.boolean.opBoolean","COPY",EDGE,{"derivedFrom":makeQuery(id+"F8.opExtrude","CAP_EDGE",EDGE,{"disambiguationData":[OSD([sQuery(id+"F6.wireOp",EDGE,"E54.0")])],"isStart":true})});
            var Q17;
            Q17=makeQuery(id+"F8.boolean.opBoolean","COPY",EDGE,{"derivedFrom":makeQuery(id+"F8.opExtrude","CAP_EDGE",EDGE,{"disambiguationData":[OSD([sQuery(id+"F6.wireOp",EDGE,"E54.3")])],"isStart":true})});
            var Q18;
            Q18=makeQuery(id+"F8.boolean.opBoolean","COPY",EDGE,{"derivedFrom":makeQuery(id+"F8.opExtrude","CAP_EDGE",EDGE,{"disambiguationData":[OSD([sQuery(id+"F6.wireOp",EDGE,"E54.2")])],"isStart":true})});
            var Q19;
            Q19=makeQuery(id+"F8.boolean.opBoolean","COPY",EDGE,{"derivedFrom":makeQuery(id+"F8.opExtrude","CAP_EDGE",EDGE,{"disambiguationData":[OSD([sQuery(id+"F6.wireOp",EDGE,"E54.1")])],"isStart":true})});
            var Q20;
            Q20=makeQuery(id+"F7.opExtrude","CAP_EDGE",EDGE,{"disambiguationData":[OSD([sQuery(id+"F6.wireOp",EDGE,"E56")])],"isStart":true});
            var Q21;
            Q21=makeQuery(id+"F7.opExtrude","CAP_EDGE",EDGE,{"disambiguationData":[OSD([sQuery(id+"F6.wireOp",EDGE,"E59")])],"isStart":true});
            fillet(context, id + "F10", {"entities" : qUnion([Q0, Q1, Q2, Q3, Q4, Q5, Q6, Q7, Q8, Q9, Q10, Q11, Q12, Q13, Q14, Q15, Q16, Q17, Q18, Q19, Q20, Q21]), "radius" : .5 * mm, "tangentPropagation" : true, "allowEdgeOverflow" : false});
        }
    });
